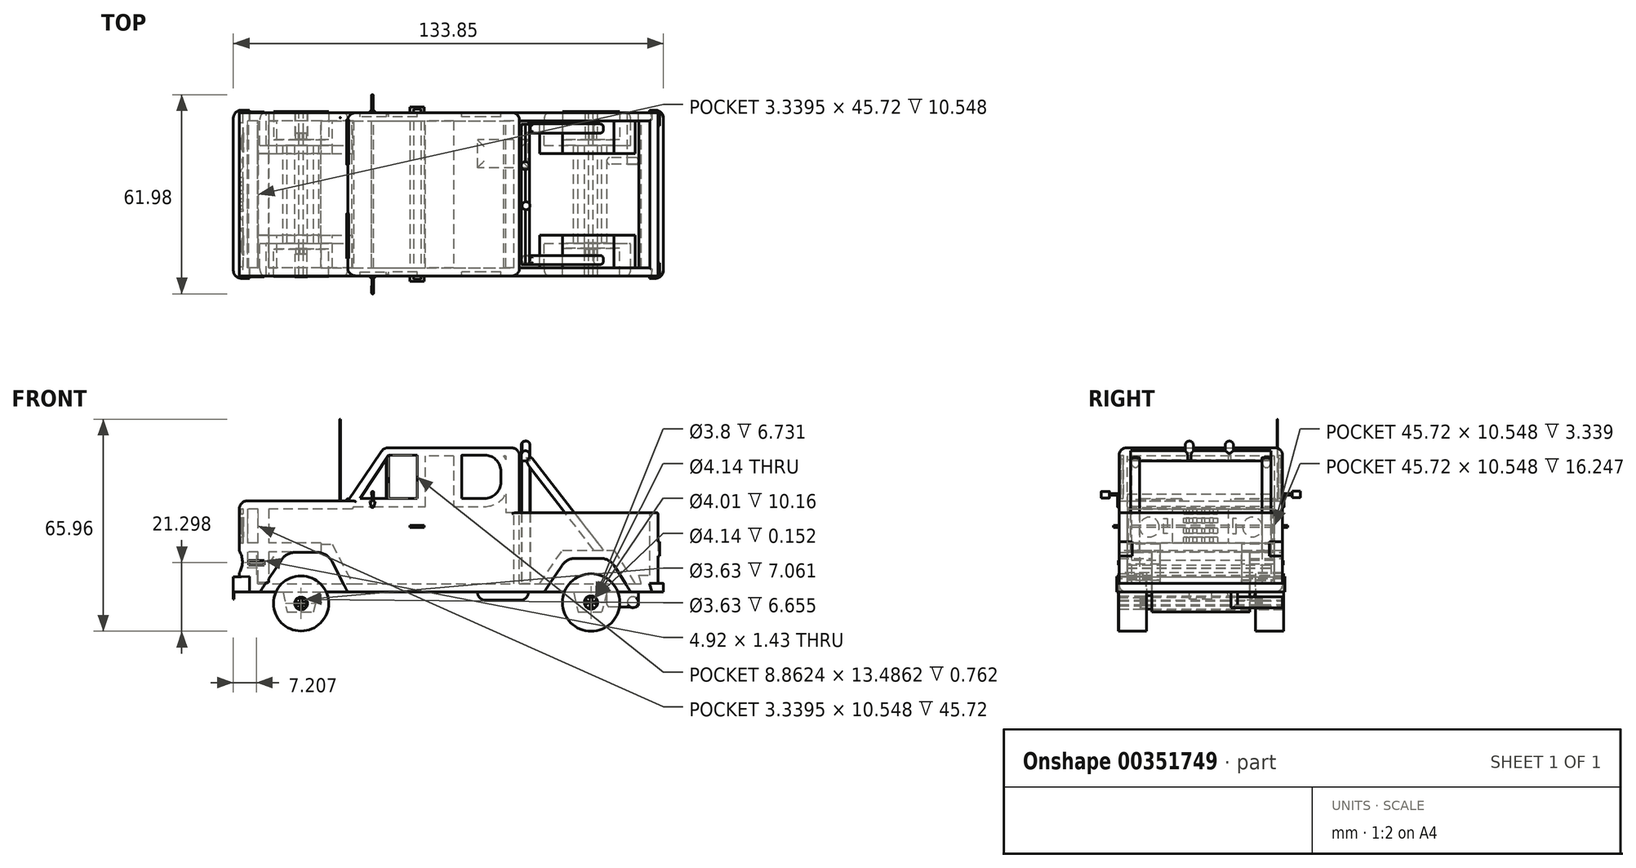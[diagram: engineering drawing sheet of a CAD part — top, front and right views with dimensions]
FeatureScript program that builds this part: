
annotation { "Feature Type Name" : "Feature", "Feature Type Description" : "" }
export const myFeature = defineFeature(function(context is Context, id is Id, definition is map)
    precondition{}
    {
        {
            var Q0;
            Q0=qCreatedBy(makeId("Front.planeOp"),FACE);
            var sketch = newSketch(context, id + "F0", { "sketchPlane" : qUnion([Q0])});
            skLineSegment(sketch, "E0", {"start": v(0, 0) * mm, "end": v(61.08, 0) * mm});
            skLineSegment(sketch, "E1", {"start": v(61.08, 0) * mm, "end": v(68.16, 10.52) * mm});
            skLineSegment(sketch, "E2", {"start": v(68.16, 10.52) * mm, "end": v(81.45, 10.52) * mm});
            skLineSegment(sketch, "E3", {"start": v(81.45, 10.52) * mm, "end": v(88.1, 0) * mm});
            skLineSegment(sketch, "E4", {"start": v(88.1, 0) * mm, "end": v(96.5, 0) * mm});
            skLineSegment(sketch, "E5", {"start": v(96.5, 0) * mm, "end": v(96.5, 24.7) * mm});
            skLineSegment(sketch, "E6", {"start": v(96.5, 24.7) * mm, "end": v(51.78, 24.7) * mm});
            skLineSegment(sketch, "E7", {"start": v(51.78, 44.9) * mm, "end": v(11.24, 44.9) * mm});
            skLineSegment(sketch, "E8", {"start": v(11.24, 44.9) * mm, "end": v(0, 28.4) * mm});
            skLineSegment(sketch, "E9", {"start": v(0, 28.4) * mm, "end": v(-33.75, 28.4) * mm});
            skLineSegment(sketch, "E10", {"start": v(-33.75, 28.4) * mm, "end": v(-33.75, 0) * mm});
            skLineSegment(sketch, "E11", {"start": v(-33.75, 0) * mm, "end": v(-27.38, 0) * mm});
            skLineSegment(sketch, "E12", {"start": v(-27.38, 0) * mm, "end": v(-19.06, 12.35) * mm});
            skPoint(sketch, "E12.endSnap0", {"position": v(96.5, 12.35) * mm});
            skLineSegment(sketch, "E13", {"start": v(-19.06, 12.35) * mm, "end": v(-6.38, 12.35) * mm});
            skLineSegment(sketch, "E14", {"start": v(-6.38, 12.35) * mm, "end": v(0, 0) * mm});
            skLineSegment(sketch, "E15", {"start": v(51.78, 44.9) * mm, "end": v(51.78, 0) * mm});
            skLineSegment(sketch, "E16", {"start": v(61.08, 0) * mm, "end": v(88.1, 0) * mm});
            skLineSegment(sketch, "E17", {"start": v(-27.38, 0) * mm, "end": v(0, 0) * mm});
            skLineSegment(sketch, "E18", {"start": v(93.9, 2.7) * mm, "end": v(98.24, 2.7) * mm});
            skLineSegment(sketch, "E19", {"start": v(98.24, 0) * mm, "end": v(94.66, 0) * mm});
            skLineSegment(sketch, "E20", {"start": v(94.66, 0) * mm, "end": v(93.9, 2.7) * mm});
            skArc(sketch, "E21", {"start": v(98.24, 2.7) * mm, "mid": v(98.15, 1.35) * mm, "end": v(98.24, 0) * mm});
            skLineSegment(sketch, "E22", {"start": v(-33.75, 4.77) * mm, "end": v(-35.61, 4.77) * mm});
            skLineSegment(sketch, "E23", {"start": v(-35.61, 4.77) * mm, "end": v(-35.61, 0) * mm});
            skLineSegment(sketch, "E24", {"start": v(-35.61, 0) * mm, "end": v(-30.56, 0) * mm});
            skLineSegment(sketch, "E25", {"start": v(-30.56, 0) * mm, "end": v(-30.56, 4.9) * mm});
            skLineSegment(sketch, "E26", {"start": v(-30.56, 4.9) * mm, "end": v(-33.75, 4.77) * mm});
            skLineSegment(sketch, "E27", {"start": v(12.77, 42.65) * mm, "end": v(3.9, 29.17) * mm});
            skLineSegment(sketch, "E28", {"start": v(3.9, 29.17) * mm, "end": v(21.63, 29.17) * mm});
            skLineSegment(sketch, "E29", {"start": v(21.63, 29.17) * mm, "end": v(21.63, 42.65) * mm});
            skLineSegment(sketch, "E30", {"start": v(21.63, 42.65) * mm, "end": v(12.77, 42.65) * mm});
            skLineSegment(sketch, "E31", {"start": v(35.5, 42.65) * mm, "end": v(35.5, 29.17) * mm});
            skLineSegment(sketch, "E32", {"start": v(35.5, 29.17) * mm, "end": v(42.56, 29.17) * mm});
            skLineSegment(sketch, "E33", {"start": v(47.64, 34.25) * mm, "end": v(47.64, 37.57) * mm});
            skLineSegment(sketch, "E34", {"start": v(42.56, 42.65) * mm, "end": v(35.5, 42.65) * mm});
            skPoint(sketch, "E35.visualSharp", {"position": v(47.64, 42.65) * mm});
            skArc(sketch, "E35.filletArc", {"start": v(47.64, 37.57) * mm, "mid": v(46.15, 41.17) * mm, "end": v(42.56, 42.65) * mm});
            skPoint(sketch, "E36.visualSharp", {"position": v(47.64, 29.17) * mm});
            skArc(sketch, "E36.filletArc", {"start": v(42.56, 29.17) * mm, "mid": v(46.15, 30.66) * mm, "end": v(47.64, 34.25) * mm});
            skSolve(sketch);
        }
        {
            var Q0;
            {var subQ2=sQuery(id+"F0.wireOp",EDGE,"E7");Q0=makeQuery(id+"F0.imprint","IMPRINT",FACE,{"disambiguationData":[TD([[makeQuery(id+"F0.imprint","IMPRINT",EDGE,{"derivedFrom":subQ2}),1.0]])]});}
            var Q1;
            {var subQ0=sQuery(id+"F0.wireOp",EDGE,"E1");Q1=makeQuery(id+"F0.imprint","IMPRINT",FACE,{"disambiguationData":[TD([[makeQuery(id+"F0.imprint","IMPRINT",EDGE,{"derivedFrom":subQ0}),1.0]])]});}
            extrude(context, id + "F1", {"entities" : qUnion([Q0, Q1]), "depth" : 25.4 * mm});
        }
        {
            var Q0;
            {var subQ2=sQuery(id+"F0.wireOp",EDGE,"E7");Q0=makeQuery(id+"F0.imprint","IMPRINT",FACE,{"disambiguationData":[TD([[makeQuery(id+"F0.imprint","IMPRINT",EDGE,{"derivedFrom":subQ2}),1.0]])]});}
            var Q1;
            {var subQ0=sQuery(id+"F0.wireOp",EDGE,"E1");Q1=makeQuery(id+"F0.imprint","IMPRINT",FACE,{"disambiguationData":[TD([[makeQuery(id+"F0.imprint","IMPRINT",EDGE,{"derivedFrom":subQ0}),1.0]])]});}
            extrude(context, id + "F2", {"entities" : qUnion([Q0, Q1]), "operationType" : NewBodyOperationType.ADD, "oppositeDirection" : true, "depth" : 25.4 * mm});
        }
        {
            var Q0;
            Q0=makeQuery(id+"F0.imprint","IMPRINT",FACE,{"disambiguationData":[TD([[makeQuery(id+"F0.imprint","IMPRINT",EDGE,{"derivedFrom":sQuery(id+"F0.wireOp",EDGE,"E12")}),-1.0]])]});
            var Q1;
            Q1=makeQuery(id+"F0.imprint","IMPRINT",FACE,{"disambiguationData":[TD([[makeQuery(id+"F0.imprint","IMPRINT",EDGE,{"derivedFrom":sQuery(id+"F0.wireOp",EDGE,"E1")}),-1.0]])]});
            var Q2;
            Q2 = qSketchRegion(id + "F8", true);
            extrude(context, id + "F3", {"entities" : qUnion([Q0, Q1, Q2]), "operationType" : NewBodyOperationType.ADD, "depth" : 15.24 * mm});
        }
        {
            var Q0;
            Q0=makeQuery(id+"F0.imprint","IMPRINT",FACE,{"disambiguationData":[TD([[makeQuery(id+"F0.imprint","IMPRINT",EDGE,{"derivedFrom":sQuery(id+"F0.wireOp",EDGE,"E12")}),-1.0]])]});
            var Q1;
            Q1=makeQuery(id+"F0.imprint","IMPRINT",FACE,{"disambiguationData":[TD([[makeQuery(id+"F0.imprint","IMPRINT",EDGE,{"derivedFrom":sQuery(id+"F0.wireOp",EDGE,"E1")}),-1.0]])]});
            extrude(context, id + "F4", {"entities" : qUnion([Q0, Q1]), "operationType" : NewBodyOperationType.ADD, "oppositeDirection" : true, "depth" : 15.24 * mm});
        }
        {
            var Q0;
            {var subQ0=sQuery(id+"F0.wireOp",EDGE,"E6");Q0=makeQuery(id+"F2.boolean.opBoolean","MERGE",FACE,{"derivedFrom":[makeQuery(id+"F1.opExtrude","SWEPT_FACE",FACE,{"disambiguationData":[OSD([subQ0])]}),makeQuery(id+"F2.opExtrude","SWEPT_FACE",FACE,{"disambiguationData":[OSD([subQ0])]})]});}
            shell(context, id + "F5", {"entities" : qUnion([Q0]), "thickness" : 2.54 * mm});
        }
        {
            var Q0;
            {var subQ0=sQuery(id+"F0.wireOp",EDGE,"E7");Q0=makeQuery(id+"F2.boolean.opBoolean","MERGE",FACE,{"derivedFrom":[makeQuery(id+"F1.opExtrude","SWEPT_FACE",FACE,{"disambiguationData":[OSD([subQ0])]}),makeQuery(id+"F2.opExtrude","SWEPT_FACE",FACE,{"disambiguationData":[OSD([subQ0])]})]});}
            var sketch = newSketch(context, id + "F6", { "sketchPlane" : qUnion([Q0])});
            skLineSegment(sketch, "E37", {"start": v(51.78, 25.4) * mm, "end": v(51.78, -25.4) * mm});
            skLineSegment(sketch, "E38", {"start": v(51.78, -25.4) * mm, "end": v(53.43, -25.4) * mm});
            skLineSegment(sketch, "E39", {"start": v(53.43, -25.4) * mm, "end": v(53.43, 25.4) * mm});
            skLineSegment(sketch, "E40", {"start": v(53.43, 25.4) * mm, "end": v(51.78, 25.4) * mm});
            skSolve(sketch);
        }
        {
            var Q0;
            Q0=makeQuery(id+"F6.imprint","IMPRINT",FACE,{"disambiguationData":[TD([[makeQuery(id+"F6.imprint","IMPRINT",EDGE,{"derivedFrom":sQuery(id+"F6.wireOp",EDGE,"E37")}),-1.0]])]});
            extrude(context, id + "F7", {"entities" : qUnion([Q0]), "operationType" : NewBodyOperationType.ADD, "oppositeDirection" : true, "depth" : 43.18 * mm});
        }
        {
            var Q0;
            {var subQ0=sQuery(id+"F0.wireOp",EDGE,"E5");Q0=makeQuery(id+"F2.boolean.opBoolean","MERGE",FACE,{"derivedFrom":[makeQuery(id+"F1.opExtrude","SWEPT_FACE",FACE,{"disambiguationData":[OSD([subQ0])]}),makeQuery(id+"F2.opExtrude","SWEPT_FACE",FACE,{"disambiguationData":[OSD([subQ0])]})]});}
            var sketch = newSketch(context, id + "F8", { "sketchPlane" : qUnion([Q0])});
            skLineSegment(sketch, "E41", {"start": v(25.4, 15.72) * mm, "end": v(21.36, 15.72) * mm});
            skLineSegment(sketch, "E42", {"start": v(21.36, 15.72) * mm, "end": v(21.36, 14.13) * mm});
            skLineSegment(sketch, "E43", {"start": v(21.36, 14.13) * mm, "end": v(25.4, 14.13) * mm});
            skLineSegment(sketch, "E44", {"start": v(25.4, 14.13) * mm, "end": v(25.4, 15.72) * mm});
            skLineSegment(sketch, "E45", {"start": v(25.4, 14.13) * mm, "end": v(25.4, 11.25) * mm});
            skLineSegment(sketch, "E46", {"start": v(25.4, 11.25) * mm, "end": v(21.36, 11.25) * mm});
            skLineSegment(sketch, "E47", {"start": v(21.36, 11.25) * mm, "end": v(21.36, 14.13) * mm});
            skLineSegment(sketch, "E48", {"start": v(-25.4, 15.72) * mm, "end": v(-21.36, 15.72) * mm});
            skLineSegment(sketch, "E49", {"start": v(-21.36, 15.72) * mm, "end": v(-21.36, 14.13) * mm});
            skLineSegment(sketch, "E50", {"start": v(-21.36, 14.13) * mm, "end": v(-25.4, 14.13) * mm});
            skLineSegment(sketch, "E51", {"start": v(-25.4, 14.13) * mm, "end": v(-25.4, 15.72) * mm});
            skLineSegment(sketch, "E52", {"start": v(-25.4, 14.13) * mm, "end": v(-25.4, 11.25) * mm});
            skLineSegment(sketch, "E53", {"start": v(-25.4, 11.25) * mm, "end": v(-21.36, 11.25) * mm});
            skLineSegment(sketch, "E54", {"start": v(-21.36, 11.25) * mm, "end": v(-21.36, 14.13) * mm});
            skSolve(sketch);
        }
        {
            var Q0;
            Q0=makeQuery(id+"F8.imprint","IMPRINT",FACE,{"disambiguationData":[TD([[makeQuery(id+"F8.imprint","IMPRINT",EDGE,{"derivedFrom":sQuery(id+"F8.wireOp",EDGE,"E43")}),-1.0]])]});
            var Q1;
            Q1=makeQuery(id+"F8.imprint","IMPRINT",FACE,{"disambiguationData":[TD([[makeQuery(id+"F8.imprint","IMPRINT",EDGE,{"derivedFrom":sQuery(id+"F8.wireOp",EDGE,"E41")}),1.0]])]});
            var Q2;
            Q2=makeQuery(id+"F8.imprint","IMPRINT",FACE,{"disambiguationData":[TD([[makeQuery(id+"F8.imprint","IMPRINT",EDGE,{"derivedFrom":sQuery(id+"F8.wireOp",EDGE,"E48")}),-1.0]])]});
            var Q3;
            Q3=makeQuery(id+"F8.imprint","IMPRINT",FACE,{"disambiguationData":[TD([[makeQuery(id+"F8.imprint","IMPRINT",EDGE,{"derivedFrom":sQuery(id+"F8.wireOp",EDGE,"E50")}),1.0]])]});
            extrude(context, id + "F9", {"entities" : qUnion([Q0, Q1, Q2, Q3]), "operationType" : NewBodyOperationType.ADD, "depth" : 0.5 * mm});
        }
        {
            var Q0;
            {var subQ5=sQuery(id+"F0.wireOp",EDGE,"E21");Q0=makeQuery(id+"F0.imprint","IMPRINT",FACE,{"disambiguationData":[TD([[makeQuery(id+"F0.imprint","IMPRINT",EDGE,{"derivedFrom":subQ5}),-1.0]])]});}
            var Q1;
            {var subQ5=sQuery(id+"F0.wireOp",EDGE,"E20");Q1=makeQuery(id+"F0.imprint","IMPRINT",FACE,{"disambiguationData":[TD([[makeQuery(id+"F0.imprint","IMPRINT",EDGE,{"derivedFrom":subQ5}),-1.0]])]});}
            extrude(context, id + "F10", {"entities" : qUnion([Q0, Q1]), "operationType" : NewBodyOperationType.ADD, "depth" : 26.16 * mm});
        }
        {
            var Q0;
            {var subQ5=sQuery(id+"F0.wireOp",EDGE,"E20");Q0=makeQuery(id+"F0.imprint","IMPRINT",FACE,{"disambiguationData":[TD([[makeQuery(id+"F0.imprint","IMPRINT",EDGE,{"derivedFrom":subQ5}),-1.0]])]});}
            var Q1;
            {var subQ5=sQuery(id+"F0.wireOp",EDGE,"E21");Q1=makeQuery(id+"F0.imprint","IMPRINT",FACE,{"disambiguationData":[TD([[makeQuery(id+"F0.imprint","IMPRINT",EDGE,{"derivedFrom":subQ5}),-1.0]])]});}
            extrude(context, id + "F11", {"entities" : qUnion([Q0, Q1]), "operationType" : NewBodyOperationType.ADD, "oppositeDirection" : true, "depth" : 26.16 * mm});
        }
        {
            var Q0;
            Q0=makeQuery(id+"F11.opExtrude","CAP_EDGE",EDGE,{"disambiguationData":[OSD([sQuery(id+"F0.wireOp",EDGE,"E21")])],"isStart":false});
            var Q1;
            Q1=makeQuery(id+"F10.opExtrude","CAP_EDGE",EDGE,{"disambiguationData":[OSD([sQuery(id+"F0.wireOp",EDGE,"E21")])],"isStart":false});
            fillet(context, id + "F12", {"entities" : qUnion([Q0, Q1]), "radius" : 2.54 * mm, "tangentPropagation" : true, "allowEdgeOverflow" : false});
        }
        {
            var Q0;
            {var subQ4=sQuery(id+"F0.wireOp",EDGE,"E25");Q0=makeQuery(id+"F0.imprint","IMPRINT",FACE,{"disambiguationData":[TD([[makeQuery(id+"F0.imprint","IMPRINT",EDGE,{"derivedFrom":subQ4}),1.0]])]});}
            var Q1;
            {var subQ3=sQuery(id+"F0.wireOp",EDGE,"E22");Q1=makeQuery(id+"F0.imprint","IMPRINT",FACE,{"disambiguationData":[TD([[makeQuery(id+"F0.imprint","IMPRINT",EDGE,{"derivedFrom":subQ3}),1.0]])]});}
            extrude(context, id + "F13", {"entities" : qUnion([Q0, Q1]), "operationType" : NewBodyOperationType.ADD, "depth" : 26.16 * mm});
        }
        {
            var Q0;
            {var subQ4=sQuery(id+"F0.wireOp",EDGE,"E25");Q0=makeQuery(id+"F0.imprint","IMPRINT",FACE,{"disambiguationData":[TD([[makeQuery(id+"F0.imprint","IMPRINT",EDGE,{"derivedFrom":subQ4}),1.0]])]});}
            var Q1;
            {var subQ3=sQuery(id+"F0.wireOp",EDGE,"E22");Q1=makeQuery(id+"F0.imprint","IMPRINT",FACE,{"disambiguationData":[TD([[makeQuery(id+"F0.imprint","IMPRINT",EDGE,{"derivedFrom":subQ3}),1.0]])]});}
            extrude(context, id + "F14", {"entities" : qUnion([Q0, Q1]), "operationType" : NewBodyOperationType.ADD, "oppositeDirection" : true, "depth" : 26.16 * mm});
        }
        {
            var Q0;
            Q0=makeQuery(id+"F14.opExtrude","CAP_EDGE",EDGE,{"disambiguationData":[OSD([sQuery(id+"F0.wireOp",EDGE,"E23")])],"isStart":false});
            var Q1;
            Q1=makeQuery(id+"F13.opExtrude","CAP_EDGE",EDGE,{"disambiguationData":[OSD([sQuery(id+"F0.wireOp",EDGE,"E23")])],"isStart":false});
            fillet(context, id + "F15", {"entities" : qUnion([Q0, Q1]), "radius" : 2.54 * mm, "tangentPropagation" : true, "allowEdgeOverflow" : false});
        }
        {
            var Q0;
            Q0=makeQuery(id+"F7.opExtrude","CAP_EDGE",EDGE,{"disambiguationData":[OSD([sQuery(id+"F6.wireOp",EDGE,"E39")])],"isStart":true});
            var Q1;
            {var subQ0=sQuery(id+"F0.wireOp",EDGE,"E8");var subQ1=sQuery(id+"F0.wireOp",EDGE,"E7");Q1=makeQuery(id+"F2.boolean.opBoolean","MERGE",EDGE,{"derivedFrom":[makeQuery(id+"F1.opExtrude","SWEPT_EDGE",EDGE,{"disambiguationData":[OSD([subQ1,subQ0])]}),makeQuery(id+"F2.opExtrude","SWEPT_EDGE",EDGE,{"disambiguationData":[OSD([subQ1,subQ0])]})]});}
            var Q2;
            {var subQ0=sQuery(id+"F0.wireOp",EDGE,"E10");var subQ1=sQuery(id+"F0.wireOp",EDGE,"E9");Q2=makeQuery(id+"F2.boolean.opBoolean","MERGE",EDGE,{"derivedFrom":[makeQuery(id+"F1.opExtrude","SWEPT_EDGE",EDGE,{"disambiguationData":[OSD([subQ1,subQ0])]}),makeQuery(id+"F2.opExtrude","SWEPT_EDGE",EDGE,{"disambiguationData":[OSD([subQ1,subQ0])]})]});}
            fillet(context, id + "F16", {"entities" : qUnion([Q0, Q1, Q2]), "radius" : 2.54 * mm, "tangentPropagation" : true, "allowEdgeOverflow" : false});
        }
        {
            var Q0;
            Q0=makeQuery(id+"F0.imprint","IMPRINT",FACE,{"disambiguationData":[TD([[makeQuery(id+"F0.imprint","IMPRINT",EDGE,{"derivedFrom":sQuery(id+"F0.wireOp",EDGE,"E27")}),1.0]])]});
            var Q1;
            Q1=makeQuery(id+"F0.imprint","IMPRINT",FACE,{"disambiguationData":[TD([[makeQuery(id+"F0.imprint","IMPRINT",EDGE,{"derivedFrom":sQuery(id+"F0.wireOp",EDGE,"E31")}),1.0]])]});
            extrude(context, id + "F17", {"entities" : qUnion([Q0, Q1]), "operationType" : NewBodyOperationType.ADD, "oppositeDirection" : true, "depth" : 24.13 * mm});
        }
        {
            var Q0;
            Q0=makeQuery(id+"F0.imprint","IMPRINT",FACE,{"disambiguationData":[TD([[makeQuery(id+"F0.imprint","IMPRINT",EDGE,{"derivedFrom":sQuery(id+"F0.wireOp",EDGE,"E27")}),1.0]])]});
            var Q1;
            Q1=makeQuery(id+"F0.imprint","IMPRINT",FACE,{"disambiguationData":[TD([[makeQuery(id+"F0.imprint","IMPRINT",EDGE,{"derivedFrom":sQuery(id+"F0.wireOp",EDGE,"E31")}),1.0]])]});
            extrude(context, id + "F18", {"entities" : qUnion([Q0, Q1]), "operationType" : NewBodyOperationType.ADD, "depth" : 24.13 * mm});
        }
        {
            var Q0;
            {var subQ0=sQuery(id+"F0.wireOp",EDGE,"E10");Q0=makeQuery(id+"F2.boolean.opBoolean","MERGE",FACE,{"derivedFrom":[makeQuery(id+"F1.opExtrude","SWEPT_FACE",FACE,{"disambiguationData":[OSD([subQ0])]}),makeQuery(id+"F2.opExtrude","SWEPT_FACE",FACE,{"disambiguationData":[OSD([subQ0])]})]});}
            var sketch = newSketch(context, id + "F19", { "sketchPlane" : qUnion([Q0])});
            skLineSegment(sketch, "E55.top", {"start": v(-25.4, 25.86) * mm, "end": v(25.4, 25.86) * mm});
            skLineSegment(sketch, "E56", {"start": v(25.4, 25.86) * mm, "end": v(25.4, 15.31) * mm});
            skLineSegment(sketch, "E57", {"start": v(25.4, 15.31) * mm, "end": v(-25.4, 15.31) * mm});
            skLineSegment(sketch, "E58", {"start": v(-25.4, 15.31) * mm, "end": v(-25.4, 25.86) * mm});
            skSolve(sketch);
        }
        {
            var Q0;
            Q0=makeQuery(id+"F19.imprint","IMPRINT",FACE,{"disambiguationData":[TD([[makeQuery(id+"F19.imprint","IMPRINT",EDGE,{"derivedFrom":sQuery(id+"F19.wireOp",EDGE,"E55.top")}),1.0]])]});
            extrude(context, id + "F20", {"entities" : qUnion([Q0]), "operationType" : NewBodyOperationType.REMOVE, "oppositeDirection" : true, "depth" : 1.27 * mm});
        }
        {
            var Q0;
            {var subQ0=sQuery(id+"F0.wireOp",EDGE,"E9");Q0=makeQuery(id+"F2.boolean.opBoolean","MERGE",FACE,{"derivedFrom":[makeQuery(id+"F1.opExtrude","SWEPT_FACE",FACE,{"disambiguationData":[OSD([subQ0])]}),makeQuery(id+"F2.opExtrude","SWEPT_FACE",FACE,{"disambiguationData":[OSD([subQ0])]})]});}
            var sketch = newSketch(context, id + "F21", { "sketchPlane" : qUnion([Q0])});
            skLineSegment(sketch, "E59", {"start": v(-27.87, -25.4) * mm, "end": v(-27.87, 25.4) * mm});
            skLineSegment(sketch, "E60", {"start": v(-27.87, 25.4) * mm, "end": v(-24.6, 25.4) * mm});
            skLineSegment(sketch, "E61", {"start": v(-24.6, 25.4) * mm, "end": v(-24.6, -25.4) * mm});
            skLineSegment(sketch, "E62", {"start": v(-24.6, -25.4) * mm, "end": v(-27.87, -25.4) * mm});
            skSolve(sketch);
        }
        {
            var Q0;
            Q0=makeQuery(id+"F21.imprint","IMPRINT",FACE,{"disambiguationData":[TD([[makeQuery(id+"F21.imprint","IMPRINT",EDGE,{"derivedFrom":sQuery(id+"F21.wireOp",EDGE,"E59")}),-1.0]])]});
            extrude(context, id + "F22", {"entities" : qUnion([Q0]), "operationType" : NewBodyOperationType.ADD, "oppositeDirection" : true, "depth" : 25.4 * mm});
        }
        {
            var Q0;
            {var subQ0=sQuery(id+"F0.wireOp",EDGE,"E10");Q0=makeQuery(id+"F2.boolean.opBoolean","MERGE",FACE,{"derivedFrom":[makeQuery(id+"F1.opExtrude","SWEPT_FACE",FACE,{"disambiguationData":[OSD([subQ0])]}),makeQuery(id+"F2.opExtrude","SWEPT_FACE",FACE,{"disambiguationData":[OSD([subQ0])]})]});}
            var sketch = newSketch(context, id + "F23", { "sketchPlane" : qUnion([Q0])});
            skLineSegment(sketch, "E63", {"start": v(-25.4, 15.31) * mm, "end": v(25.4, 15.31) * mm});
            skLineSegment(sketch, "E64", {"start": v(25.4, 15.31) * mm, "end": v(25.4, 12.44) * mm});
            skLineSegment(sketch, "E65", {"start": v(25.4, 12.44) * mm, "end": v(-25.4, 12.44) * mm});
            skLineSegment(sketch, "E66", {"start": v(-25.4, 12.44) * mm, "end": v(-25.4, 15.31) * mm});
            skSolve(sketch);
        }
        {
            var Q0;
            Q0=makeQuery(id+"F23.imprint","IMPRINT",FACE,{"disambiguationData":[TD([[makeQuery(id+"F23.imprint","IMPRINT",EDGE,{"derivedFrom":sQuery(id+"F23.wireOp",EDGE,"E63")}),1.0]])]});
            extrude(context, id + "F24", {"entities" : qUnion([Q0]), "operationType" : NewBodyOperationType.ADD, "oppositeDirection" : true, "depth" : 25.4 * mm});
        }
        {
            var Q0;
            Q0=makeQuery(id+"F20.boolean.opBoolean","COPY",FACE,{"derivedFrom":makeQuery(id+"F20.opExtrude","CAP_FACE",FACE,{"disambiguationData":[OSD([sQuery(id+"F19.wireOp",EDGE,"E55.top"),sQuery(id+"F19.wireOp",EDGE,"E56"),sQuery(id+"F19.wireOp",EDGE,"E57"),sQuery(id+"F19.wireOp",EDGE,"E58")])],"isStart":false})});
            var sketch = newSketch(context, id + "F25", { "sketchPlane" : qUnion([Q0])});
            skLineSegment(sketch, "E67", {"start": v(25.4, 25.86) * mm, "end": v(25.4, 15.31) * mm});
            skLineSegment(sketch, "E68", {"start": v(25.4, 15.31) * mm, "end": v(22.54, 15.31) * mm});
            skLineSegment(sketch, "E69", {"start": v(22.54, 15.31) * mm, "end": v(22.54, 25.86) * mm});
            skLineSegment(sketch, "E70", {"start": v(22.54, 25.86) * mm, "end": v(25.4, 25.86) * mm});
            skLineSegment(sketch, "E71", {"start": v(-25.4, 25.86) * mm, "end": v(-22.36, 25.86) * mm});
            skLineSegment(sketch, "E72", {"start": v(-22.36, 25.86) * mm, "end": v(-22.36, 15.31) * mm});
            skLineSegment(sketch, "E73", {"start": v(-22.36, 15.31) * mm, "end": v(-25.4, 15.31) * mm});
            skLineSegment(sketch, "E74", {"start": v(-25.4, 15.31) * mm, "end": v(-25.4, 25.86) * mm});
            skLineSegment(sketch, "E75", {"start": v(8.71, 25.86) * mm, "end": v(-8.54, 25.86) * mm});
            skLineSegment(sketch, "E76", {"start": v(-8.54, 25.86) * mm, "end": v(-8.54, 15.31) * mm});
            skLineSegment(sketch, "E77", {"start": v(-8.54, 15.31) * mm, "end": v(8.71, 15.31) * mm});
            skLineSegment(sketch, "E78", {"start": v(8.71, 15.31) * mm, "end": v(8.71, 25.86) * mm});
            skSolve(sketch);
        }
        {
            var Q0;
            Q0=makeQuery(id+"F25.imprint","IMPRINT",FACE,{"disambiguationData":[TD([[makeQuery(id+"F25.imprint","IMPRINT",EDGE,{"derivedFrom":sQuery(id+"F25.wireOp",EDGE,"E75")}),1.0]])]});
            var Q1;
            Q1=makeQuery(id+"F25.imprint","IMPRINT",FACE,{"disambiguationData":[TD([[makeQuery(id+"F25.imprint","IMPRINT",EDGE,{"derivedFrom":sQuery(id+"F25.wireOp",EDGE,"E71")}),1.0]])]});
            var Q2;
            Q2=makeQuery(id+"F25.imprint","IMPRINT",FACE,{"disambiguationData":[TD([[makeQuery(id+"F25.imprint","IMPRINT",EDGE,{"derivedFrom":sQuery(id+"F25.wireOp",EDGE,"E67")}),-1.0]])]});
            extrude(context, id + "F26", {"entities" : qUnion([Q0, Q1, Q2]), "operationType" : NewBodyOperationType.ADD, "depth" : 1.27 * mm});
        }
        {
            var Q0;
            Q0=makeQuery(id+"F26.opExtrude","CAP_EDGE",EDGE,{"disambiguationData":[OSD([sQuery(id+"F25.wireOp",EDGE,"E78")])],"isStart":false});
            var Q1;
            Q1=makeQuery(id+"F26.opExtrude","CAP_EDGE",EDGE,{"disambiguationData":[OSD([sQuery(id+"F25.wireOp",EDGE,"E76")])],"isStart":false});
            fillet(context, id + "F27", {"entities" : qUnion([Q0, Q1]), "radius" : 5.08 * mm, "tangentPropagation" : true, "allowEdgeOverflow" : false});
        }
        {
            var Q0;
            {var subQ0=sQuery(id+"F19.wireOp",EDGE,"E55.top");var subQ1=sQuery(id+"F19.wireOp",EDGE,"E57");Q0=makeQuery(id+"F26.boolean.opBoolean","SPLIT",FACE,{"disambiguationData":[TD([makeQuery(id+"F26.opExtrude","SWEPT_FACE",FACE,{"disambiguationData":[OSD([sQuery(id+"F25.wireOp",EDGE,"E72")])]})])],"derivedFrom":makeQuery(id+"F20.boolean.opBoolean","COPY",FACE,{"derivedFrom":makeQuery(id+"F20.opExtrude","CAP_FACE",FACE,{"disambiguationData":[OSD([subQ0,sQuery(id+"F19.wireOp",EDGE,"E56"),subQ1,sQuery(id+"F19.wireOp",EDGE,"E58")])],"isStart":false})})});}
            var sketch = newSketch(context, id + "F28", { "sketchPlane" : qUnion([Q0])});
            skCircle(sketch, "E79", {"center": v(-16.07, 20.25) * mm, "radius": 3.06 * mm});
            skCircle(sketch, "E80", {"center": v(15.98, 20.25) * mm, "radius": 3.07 * mm});
            skLineSegment(sketch, "E81", {"start": v(11.56, 22.94) * mm, "end": v(10.42, 22.94) * mm});
            skLineSegment(sketch, "E82", {"start": v(10.42, 22.94) * mm, "end": v(10.42, 18.22) * mm});
            skLineSegment(sketch, "E83", {"start": v(10.42, 18.22) * mm, "end": v(11.56, 18.22) * mm});
            skLineSegment(sketch, "E84", {"start": v(11.56, 18.22) * mm, "end": v(11.56, 22.94) * mm});
            skLineSegment(sketch, "E85", {"start": v(-9.85, 22.94) * mm, "end": v(-9.85, 18.22) * mm});
            skLineSegment(sketch, "E86", {"start": v(-9.85, 18.22) * mm, "end": v(-11, 18.22) * mm});
            skLineSegment(sketch, "E87", {"start": v(-11, 18.22) * mm, "end": v(-11, 22.94) * mm});
            skLineSegment(sketch, "E88", {"start": v(-11, 22.94) * mm, "end": v(-9.85, 22.94) * mm});
            skSolve(sketch);
        }
        {
            var Q0;
            Q0=makeQuery(id+"F28.imprint","IMPRINT",FACE,{"disambiguationData":[TD([[makeQuery(id+"F28.imprint","IMPRINT",EDGE,{"derivedFrom":sQuery(id+"F28.wireOp",EDGE,"8cGmHD0W-AUDj-nJp2-IjLW-vJfDeqEBS3v5")}),1.0]])]});
            var Q1;
            Q1=makeQuery(id+"F28.imprint","IMPRINT",FACE,{"disambiguationData":[TD([[makeQuery(id+"F28.imprint","IMPRINT",EDGE,{"derivedFrom":sQuery(id+"F28.wireOp",EDGE,"9dRMdp0R-Xc4K-p7fW-M7a4-LUDvDldkzqLd")}),1.0]])]});
            var Q2;
            Q2=makeQuery(id+"F28.imprint","IMPRINT",FACE,{"disambiguationData":[TD([[makeQuery(id+"F28.imprint","IMPRINT",EDGE,{"derivedFrom":sQuery(id+"F28.wireOp",EDGE,"E79")}),1.0]])]});
            var Q3;
            Q3=makeQuery(id+"F28.imprint","IMPRINT",FACE,{"disambiguationData":[TD([[makeQuery(id+"F28.imprint","IMPRINT",EDGE,{"derivedFrom":sQuery(id+"F28.wireOp",EDGE,"E85")}),-1.0]])]});
            var Q4;
            Q4=makeQuery(id+"F28.imprint","IMPRINT",FACE,{"disambiguationData":[TD([[makeQuery(id+"F28.imprint","IMPRINT",EDGE,{"derivedFrom":sQuery(id+"F28.wireOp",EDGE,"E81")}),1.0]])]});
            var Q5;
            Q5=makeQuery(id+"F28.imprint","IMPRINT",FACE,{"disambiguationData":[TD([[makeQuery(id+"F28.imprint","IMPRINT",EDGE,{"derivedFrom":sQuery(id+"F28.wireOp",EDGE,"E80")}),1.0]])]});
            extrude(context, id + "F29", {"entities" : qUnion([Q0, Q1, Q2, Q3, Q4, Q5]), "operationType" : NewBodyOperationType.ADD, "depth" : 0.5 * mm});
        }
        {
            var Q0;
            Q0=makeQuery(id+"F29.opExtrude","CAP_EDGE",EDGE,{"disambiguationData":[OSD([sQuery(id+"F28.wireOp",EDGE,"E80")])],"isStart":false});
            var Q1;
            Q1=makeQuery(id+"F29.opExtrude","CAP_EDGE",EDGE,{"disambiguationData":[OSD([sQuery(id+"F28.wireOp",EDGE,"E79")])],"isStart":false});
            fillet(context, id + "F30", {"entities" : qUnion([Q0, Q1]), "radius" : 2.54 * mm, "tangentPropagation" : true, "allowEdgeOverflow" : false});
        }
        {
            var Q0;
            {var subQ0=sQuery(id+"F0.wireOp",EDGE,"E10");Q0=makeQuery(id+"F26.boolean.opBoolean","MERGE",FACE,{"derivedFrom":[makeQuery(id+"F2.boolean.opBoolean","MERGE",FACE,{"derivedFrom":[makeQuery(id+"F1.opExtrude","SWEPT_FACE",FACE,{"disambiguationData":[OSD([subQ0])]}),makeQuery(id+"F2.opExtrude","SWEPT_FACE",FACE,{"disambiguationData":[OSD([subQ0])]})]}),makeQuery(id+"F26.opExtrude","CAP_FACE",FACE,{"disambiguationData":[OSD([sQuery(id+"F25.wireOp",EDGE,"E67"),sQuery(id+"F25.wireOp",EDGE,"E68"),sQuery(id+"F25.wireOp",EDGE,"E69"),sQuery(id+"F25.wireOp",EDGE,"E70")])],"isStart":false}),makeQuery(id+"F26.opExtrude","CAP_FACE",FACE,{"disambiguationData":[OSD([sQuery(id+"F25.wireOp",EDGE,"E71"),sQuery(id+"F25.wireOp",EDGE,"E72"),sQuery(id+"F25.wireOp",EDGE,"E73"),sQuery(id+"F25.wireOp",EDGE,"E74")])],"isStart":false}),makeQuery(id+"F26.opExtrude","CAP_FACE",FACE,{"disambiguationData":[OSD([sQuery(id+"F25.wireOp",EDGE,"E75"),sQuery(id+"F25.wireOp",EDGE,"E76"),sQuery(id+"F25.wireOp",EDGE,"E77"),sQuery(id+"F25.wireOp",EDGE,"E78")])],"isStart":false})]});}
            var sketch = newSketch(context, id + "F31", { "sketchPlane" : qUnion([Q0])});
            skLineSegment(sketch, "E89", {"start": v(-5.18, 25.86) * mm, "end": v(5.35, 25.86) * mm});
            skLineSegment(sketch, "E90", {"start": v(5.35, 25.86) * mm, "end": v(5.35, 24.3) * mm});
            skLineSegment(sketch, "E91", {"start": v(5.35, 24.3) * mm, "end": v(-5.18, 24.3) * mm});
            skLineSegment(sketch, "E92", {"start": v(-5.18, 24.3) * mm, "end": v(-5.18, 25.86) * mm});
            skLineSegment(sketch, "E93", {"start": v(5.35, 23.01) * mm, "end": v(-5.18, 23.01) * mm});
            skLineSegment(sketch, "E94", {"start": v(-5.18, 23.01) * mm, "end": v(-5.18, 21.46) * mm});
            skLineSegment(sketch, "E95", {"start": v(-5.18, 21.46) * mm, "end": v(5.35, 21.46) * mm});
            skLineSegment(sketch, "E96", {"start": v(5.35, 21.46) * mm, "end": v(5.35, 23.01) * mm});
            skLineSegment(sketch, "E97", {"start": v(-5.18, 19.91) * mm, "end": v(5.35, 19.91) * mm});
            skLineSegment(sketch, "E98", {"start": v(5.35, 19.91) * mm, "end": v(5.35, 18.36) * mm});
            skLineSegment(sketch, "E99", {"start": v(5.35, 18.36) * mm, "end": v(-5.18, 18.36) * mm});
            skLineSegment(sketch, "E100", {"start": v(-5.18, 18.36) * mm, "end": v(-5.18, 19.91) * mm});
            skLineSegment(sketch, "E101", {"start": v(-5.18, 17.07) * mm, "end": v(5.35, 17.07) * mm});
            skLineSegment(sketch, "E102", {"start": v(5.35, 17.07) * mm, "end": v(5.35, 15.31) * mm});
            skLineSegment(sketch, "E103", {"start": v(5.35, 15.31) * mm, "end": v(-5.18, 15.31) * mm});
            skLineSegment(sketch, "E104", {"start": v(-5.18, 15.31) * mm, "end": v(-5.18, 17.07) * mm});
            skSolve(sketch);
        }
        {
            var Q0;
            Q0=makeQuery(id+"F31.imprint","IMPRINT",FACE,{"disambiguationData":[TD([[makeQuery(id+"F31.imprint","IMPRINT",EDGE,{"derivedFrom":sQuery(id+"F31.wireOp",EDGE,"E89")}),1.0]])]});
            var Q1;
            Q1=makeQuery(id+"F31.imprint","IMPRINT",FACE,{"disambiguationData":[TD([[makeQuery(id+"F31.imprint","IMPRINT",EDGE,{"derivedFrom":sQuery(id+"F31.wireOp",EDGE,"E93")}),1.0]])]});
            var Q2;
            Q2=makeQuery(id+"F31.imprint","IMPRINT",FACE,{"disambiguationData":[TD([[makeQuery(id+"F31.imprint","IMPRINT",EDGE,{"derivedFrom":sQuery(id+"F31.wireOp",EDGE,"E97")}),-1.0]])]});
            var Q3;
            Q3=makeQuery(id+"F31.imprint","IMPRINT",FACE,{"disambiguationData":[TD([[makeQuery(id+"F31.imprint","IMPRINT",EDGE,{"derivedFrom":sQuery(id+"F31.wireOp",EDGE,"E101")}),-1.0]])]});
            extrude(context, id + "F32", {"entities" : qUnion([Q0, Q1, Q2, Q3]), "operationType" : NewBodyOperationType.REMOVE, "oppositeDirection" : true, "depth" : 1.12 * mm});
        }
        {
            var Q0;
            Q0=makeQuery(id+"F32.boolean.opBoolean","COPY",FACE,{"derivedFrom":makeQuery(id+"F32.opExtrude","CAP_FACE",FACE,{"disambiguationData":[OSD([sQuery(id+"F31.wireOp",EDGE,"E89"),sQuery(id+"F31.wireOp",EDGE,"E90"),sQuery(id+"F31.wireOp",EDGE,"E91"),sQuery(id+"F31.wireOp",EDGE,"E92")])],"isStart":false})});
            var sketch = newSketch(context, id + "F33", { "sketchPlane" : qUnion([Q0])});
            skLineSegment(sketch, "E105", {"start": v(-3.85, 25.86) * mm, "end": v(-3.85, 15.37) * mm});
            skLineSegment(sketch, "E106", {"start": v(-3.85, 15.37) * mm, "end": v(-2.81, 15.37) * mm});
            skLineSegment(sketch, "E107", {"start": v(-2.81, 15.37) * mm, "end": v(-2.81, 25.86) * mm});
            skLineSegment(sketch, "E108", {"start": v(-2.81, 25.86) * mm, "end": v(-3.85, 25.86) * mm});
            skLineSegment(sketch, "E109", {"start": v(-1.28, 25.86) * mm, "end": v(-0.24, 25.86) * mm});
            skLineSegment(sketch, "E110", {"start": v(-0.24, 25.86) * mm, "end": v(-0.24, 15.4) * mm});
            skLineSegment(sketch, "E111", {"start": v(-0.24, 15.4) * mm, "end": v(-1.28, 15.37) * mm});
            skLineSegment(sketch, "E112", {"start": v(-1.28, 15.37) * mm, "end": v(-1.28, 25.86) * mm});
            skLineSegment(sketch, "E113", {"start": v(1.28, 25.86) * mm, "end": v(1.28, 15.4) * mm});
            skLineSegment(sketch, "E114", {"start": v(1.28, 15.4) * mm, "end": v(2.36, 15.4) * mm});
            skLineSegment(sketch, "E115", {"start": v(2.36, 15.4) * mm, "end": v(2.36, 25.86) * mm});
            skLineSegment(sketch, "E116", {"start": v(2.36, 25.86) * mm, "end": v(1.28, 25.86) * mm});
            skLineSegment(sketch, "E117", {"start": v(3.5, 25.86) * mm, "end": v(4.6, 25.86) * mm});
            skLineSegment(sketch, "E118", {"start": v(4.6, 25.86) * mm, "end": v(4.6, 15.3) * mm});
            skLineSegment(sketch, "E119", {"start": v(4.6, 15.3) * mm, "end": v(3.5, 15.3) * mm});
            skLineSegment(sketch, "E120", {"start": v(3.5, 15.3) * mm, "end": v(3.5, 25.86) * mm});
            skSolve(sketch);
        }
        {
            var Q0;
            {var subQ0=sQuery(id+"F33.wireOp",EDGE,"E119");Q0=makeQuery(id+"F33.imprint","IMPRINT",FACE,{"disambiguationData":[TD([[makeQuery(id+"F33.imprint","IMPRINT",EDGE,{"derivedFrom":subQ0}),-1.0]])]});}
            var Q1;
            {var subQ0=sQuery(id+"F33.wireOp",EDGE,"E117");Q1=makeQuery(id+"F33.imprint","IMPRINT",FACE,{"disambiguationData":[TD([[makeQuery(id+"F33.imprint","IMPRINT",EDGE,{"derivedFrom":subQ0}),1.0]])]});}
            var Q2;
            {var subQ0=sQuery(id+"F33.wireOp",EDGE,"E114");Q2=makeQuery(id+"F33.imprint","IMPRINT",FACE,{"disambiguationData":[TD([[makeQuery(id+"F33.imprint","IMPRINT",EDGE,{"derivedFrom":subQ0}),1.0]])]});}
            var Q3;
            {var subQ0=sQuery(id+"F33.wireOp",EDGE,"E116");Q3=makeQuery(id+"F33.imprint","IMPRINT",FACE,{"disambiguationData":[TD([[makeQuery(id+"F33.imprint","IMPRINT",EDGE,{"derivedFrom":subQ0}),1.0]])]});}
            var Q4;
            {var subQ0=sQuery(id+"F33.wireOp",EDGE,"E109");Q4=makeQuery(id+"F33.imprint","IMPRINT",FACE,{"disambiguationData":[TD([[makeQuery(id+"F33.imprint","IMPRINT",EDGE,{"derivedFrom":subQ0}),1.0]])]});}
            var Q5;
            {var subQ0=sQuery(id+"F33.wireOp",EDGE,"E111");Q5=makeQuery(id+"F33.imprint","IMPRINT",FACE,{"disambiguationData":[TD([[makeQuery(id+"F33.imprint","IMPRINT",EDGE,{"derivedFrom":subQ0}),-1.0]])]});}
            var Q6;
            {var subQ0=sQuery(id+"F33.wireOp",EDGE,"E106");Q6=makeQuery(id+"F33.imprint","IMPRINT",FACE,{"disambiguationData":[TD([[makeQuery(id+"F33.imprint","IMPRINT",EDGE,{"derivedFrom":subQ0}),1.0]])]});}
            var Q7;
            {var subQ0=sQuery(id+"F33.wireOp",EDGE,"E108");Q7=makeQuery(id+"F33.imprint","IMPRINT",FACE,{"disambiguationData":[TD([[makeQuery(id+"F33.imprint","IMPRINT",EDGE,{"derivedFrom":subQ0}),1.0]])]});}
            extrude(context, id + "F34", {"entities" : qUnion([Q0, Q1, Q2, Q3, Q4, Q5, Q6, Q7]), "operationType" : NewBodyOperationType.ADD, "depth" : 0.69 * mm});
        }
        {
            var Q0;
            Q0=makeQuery(id+"F26.boolean.opBoolean","MERGE",FACE,{"derivedFrom":[makeQuery(id+"F22.boolean.opBoolean","MERGE",FACE,{"derivedFrom":[makeQuery(id+"F9.boolean.opBoolean","MERGE",FACE,{"derivedFrom":[makeQuery(id+"F7.boolean.opBoolean","MERGE",FACE,{"derivedFrom":[makeQuery(id+"F1.opExtrude","CAP_FACE",FACE,{"disambiguationData":[OSD([sQuery(id+"F0.wireOp",EDGE,"E0"),sQuery(id+"F0.wireOp",EDGE,"E1"),sQuery(id+"F0.wireOp",EDGE,"E2"),sQuery(id+"F0.wireOp",EDGE,"E3"),sQuery(id+"F0.wireOp",EDGE,"E4"),sQuery(id+"F0.wireOp",EDGE,"E5"),sQuery(id+"F0.wireOp",EDGE,"E6"),sQuery(id+"F0.wireOp",EDGE,"E7"),sQuery(id+"F0.wireOp",EDGE,"E8"),sQuery(id+"F0.wireOp",EDGE,"E9"),sQuery(id+"F0.wireOp",EDGE,"E10"),sQuery(id+"F0.wireOp",EDGE,"E11"),sQuery(id+"F0.wireOp",EDGE,"E12"),sQuery(id+"F0.wireOp",EDGE,"E13"),sQuery(id+"F0.wireOp",EDGE,"E14"),sQuery(id+"F0.wireOp",EDGE,"E15"),sQuery(id+"F0.wireOp",EDGE,"E18"),sQuery(id+"F0.wireOp",EDGE,"E20"),sQuery(id+"F0.wireOp",EDGE,"E25"),sQuery(id+"F0.wireOp",EDGE,"E26"),sQuery(id+"F0.wireOp",EDGE,"E27"),sQuery(id+"F0.wireOp",EDGE,"E28"),sQuery(id+"F0.wireOp",EDGE,"E29"),sQuery(id+"F0.wireOp",EDGE,"E30"),sQuery(id+"F0.wireOp",EDGE,"E31"),sQuery(id+"F0.wireOp",EDGE,"E32"),sQuery(id+"F0.wireOp",EDGE,"E33"),sQuery(id+"F0.wireOp",EDGE,"E34"),sQuery(id+"F0.wireOp",EDGE,"E35.filletArc"),sQuery(id+"F0.wireOp",EDGE,"E36.filletArc")])],"isStart":false}),makeQuery(id+"F7.opExtrude","SWEPT_FACE",FACE,{"disambiguationData":[OSD([sQuery(id+"F6.wireOp",EDGE,"E38")])]})]}),makeQuery(id+"F9.opExtrude","SWEPT_FACE",FACE,{"disambiguationData":[OSD([sQuery(id+"F8.wireOp",EDGE,"E51"),sQuery(id+"F8.wireOp",EDGE,"E52")])]})]}),makeQuery(id+"F22.opExtrude","SWEPT_FACE",FACE,{"disambiguationData":[OSD([sQuery(id+"F21.wireOp",EDGE,"E62")])]})]}),makeQuery(id+"F26.opExtrude","SWEPT_FACE",FACE,{"disambiguationData":[OSD([sQuery(id+"F25.wireOp",EDGE,"E67")])]})]});
            var sketch = newSketch(context, id + "F35", { "sketchPlane" : qUnion([Q0])});
            skArc(sketch, "E121", {"start": v(-33.75, 5.98) * mm, "mid": v(-32.78, 9.4) * mm, "end": v(-33.75, 12.83) * mm});
            skSolve(sketch);
        }
        {
            var Q0;
            {var subQ0=sQuery(id+"F35.wireOp",EDGE,"E121");Q0=makeQuery(id+"F35.imprint","IMPRINT",FACE,{"disambiguationData":[TD([[makeQuery(id+"F35.imprint","IMPRINT",EDGE,{"derivedFrom":subQ0}),1.0]])]});}
            extrude(context, id + "F36", {"entities" : qUnion([Q0]), "operationType" : NewBodyOperationType.REMOVE, "oppositeDirection" : true, "depth" : 50.8 * mm});
        }
        {
            var Q0;
            Q0=makeQuery(id+"F26.boolean.opBoolean","MERGE",FACE,{"derivedFrom":[makeQuery(id+"F22.boolean.opBoolean","MERGE",FACE,{"derivedFrom":[makeQuery(id+"F9.boolean.opBoolean","MERGE",FACE,{"derivedFrom":[makeQuery(id+"F7.boolean.opBoolean","MERGE",FACE,{"derivedFrom":[makeQuery(id+"F1.opExtrude","CAP_FACE",FACE,{"disambiguationData":[OSD([sQuery(id+"F0.wireOp",EDGE,"E0"),sQuery(id+"F0.wireOp",EDGE,"E1"),sQuery(id+"F0.wireOp",EDGE,"E2"),sQuery(id+"F0.wireOp",EDGE,"E3"),sQuery(id+"F0.wireOp",EDGE,"E4"),sQuery(id+"F0.wireOp",EDGE,"E5"),sQuery(id+"F0.wireOp",EDGE,"E6"),sQuery(id+"F0.wireOp",EDGE,"E7"),sQuery(id+"F0.wireOp",EDGE,"E8"),sQuery(id+"F0.wireOp",EDGE,"E9"),sQuery(id+"F0.wireOp",EDGE,"E10"),sQuery(id+"F0.wireOp",EDGE,"E11"),sQuery(id+"F0.wireOp",EDGE,"E12"),sQuery(id+"F0.wireOp",EDGE,"E13"),sQuery(id+"F0.wireOp",EDGE,"E14"),sQuery(id+"F0.wireOp",EDGE,"E15"),sQuery(id+"F0.wireOp",EDGE,"E18"),sQuery(id+"F0.wireOp",EDGE,"E20"),sQuery(id+"F0.wireOp",EDGE,"E25"),sQuery(id+"F0.wireOp",EDGE,"E26"),sQuery(id+"F0.wireOp",EDGE,"E27"),sQuery(id+"F0.wireOp",EDGE,"E28"),sQuery(id+"F0.wireOp",EDGE,"E29"),sQuery(id+"F0.wireOp",EDGE,"E30"),sQuery(id+"F0.wireOp",EDGE,"E31"),sQuery(id+"F0.wireOp",EDGE,"E32"),sQuery(id+"F0.wireOp",EDGE,"E33"),sQuery(id+"F0.wireOp",EDGE,"E34"),sQuery(id+"F0.wireOp",EDGE,"E35.filletArc"),sQuery(id+"F0.wireOp",EDGE,"E36.filletArc")])],"isStart":false}),makeQuery(id+"F7.opExtrude","SWEPT_FACE",FACE,{"disambiguationData":[OSD([sQuery(id+"F6.wireOp",EDGE,"E38")])]})]}),makeQuery(id+"F9.opExtrude","SWEPT_FACE",FACE,{"disambiguationData":[OSD([sQuery(id+"F8.wireOp",EDGE,"E51"),sQuery(id+"F8.wireOp",EDGE,"E52")])]})]}),makeQuery(id+"F22.opExtrude","SWEPT_FACE",FACE,{"disambiguationData":[OSD([sQuery(id+"F21.wireOp",EDGE,"E62")])]})]}),makeQuery(id+"F26.opExtrude","SWEPT_FACE",FACE,{"disambiguationData":[OSD([sQuery(id+"F25.wireOp",EDGE,"E67")])]})]});
            var sketch = newSketch(context, id + "F37", { "sketchPlane" : qUnion([Q0])});
            skLineSegment(sketch, "E122", {"start": v(56.87, 42.36) * mm, "end": v(81.45, 10.52) * mm});
            skLineSegment(sketch, "E123", {"start": v(81.45, 10.52) * mm, "end": v(78.57, 10.52) * mm});
            skLineSegment(sketch, "E124", {"start": v(78.57, 10.52) * mm, "end": v(55.44, 40.47) * mm});
            skLineSegment(sketch, "E125", {"start": v(55.44, 40.47) * mm, "end": v(56.87, 42.36) * mm});
            skSolve(sketch);
        }
        {
            var Q0;
            {var subQ0=sQuery(id+"F37.wireOp",EDGE,"E125");Q0=makeQuery(id+"F37.imprint","IMPRINT",FACE,{"disambiguationData":[TD([[makeQuery(id+"F37.imprint","IMPRINT",EDGE,{"derivedFrom":subQ0}),-1.0]])]});}
            var Q1;
            {var subQ0=sQuery(id+"F37.wireOp",EDGE,"E123");Q1=makeQuery(id+"F37.imprint","IMPRINT",FACE,{"disambiguationData":[TD([[makeQuery(id+"F37.imprint","IMPRINT",EDGE,{"derivedFrom":subQ0}),1.0]])]});}
            extrude(context, id + "F38", {"entities" : qUnion([Q0, Q1]), "operationType" : NewBodyOperationType.ADD, "oppositeDirection" : true, "depth" : 6.35 * mm, "hasSecondDirection" : true, "secondDirectionOppositeDirection" : true, "secondDirectionDepth" : 3.56 * mm});
        }
        {
            var Q0;
            {var subQ0=sQuery(id+"F37.wireOp",EDGE,"E125");Q0=makeQuery(id+"F37.imprint","IMPRINT",FACE,{"disambiguationData":[TD([[makeQuery(id+"F37.imprint","IMPRINT",EDGE,{"derivedFrom":subQ0}),-1.0]])]});}
            var Q1;
            {var subQ0=sQuery(id+"F37.wireOp",EDGE,"E123");Q1=makeQuery(id+"F37.imprint","IMPRINT",FACE,{"disambiguationData":[TD([[makeQuery(id+"F37.imprint","IMPRINT",EDGE,{"derivedFrom":subQ0}),1.0]])]});}
            extrude(context, id + "F39", {"entities" : qUnion([Q0, Q1]), "operationType" : NewBodyOperationType.ADD, "oppositeDirection" : true, "depth" : 47.27 * mm, "hasSecondDirection" : true, "secondDirectionOppositeDirection" : true, "secondDirectionDepth" : 44.45 * mm});
        }
        {
            var Q0;
            Q0=makeQuery(id+"F26.boolean.opBoolean","MERGE",FACE,{"derivedFrom":[makeQuery(id+"F22.boolean.opBoolean","MERGE",FACE,{"derivedFrom":[makeQuery(id+"F9.boolean.opBoolean","MERGE",FACE,{"derivedFrom":[makeQuery(id+"F7.boolean.opBoolean","MERGE",FACE,{"derivedFrom":[makeQuery(id+"F1.opExtrude","CAP_FACE",FACE,{"disambiguationData":[OSD([sQuery(id+"F0.wireOp",EDGE,"E0"),sQuery(id+"F0.wireOp",EDGE,"E1"),sQuery(id+"F0.wireOp",EDGE,"E2"),sQuery(id+"F0.wireOp",EDGE,"E3"),sQuery(id+"F0.wireOp",EDGE,"E4"),sQuery(id+"F0.wireOp",EDGE,"E5"),sQuery(id+"F0.wireOp",EDGE,"E6"),sQuery(id+"F0.wireOp",EDGE,"E7"),sQuery(id+"F0.wireOp",EDGE,"E8"),sQuery(id+"F0.wireOp",EDGE,"E9"),sQuery(id+"F0.wireOp",EDGE,"E10"),sQuery(id+"F0.wireOp",EDGE,"E11"),sQuery(id+"F0.wireOp",EDGE,"E12"),sQuery(id+"F0.wireOp",EDGE,"E13"),sQuery(id+"F0.wireOp",EDGE,"E14"),sQuery(id+"F0.wireOp",EDGE,"E15"),sQuery(id+"F0.wireOp",EDGE,"E18"),sQuery(id+"F0.wireOp",EDGE,"E20"),sQuery(id+"F0.wireOp",EDGE,"E25"),sQuery(id+"F0.wireOp",EDGE,"E26"),sQuery(id+"F0.wireOp",EDGE,"E27"),sQuery(id+"F0.wireOp",EDGE,"E28"),sQuery(id+"F0.wireOp",EDGE,"E29"),sQuery(id+"F0.wireOp",EDGE,"E30"),sQuery(id+"F0.wireOp",EDGE,"E31"),sQuery(id+"F0.wireOp",EDGE,"E32"),sQuery(id+"F0.wireOp",EDGE,"E33"),sQuery(id+"F0.wireOp",EDGE,"E34"),sQuery(id+"F0.wireOp",EDGE,"E35.filletArc"),sQuery(id+"F0.wireOp",EDGE,"E36.filletArc")])],"isStart":false}),makeQuery(id+"F7.opExtrude","SWEPT_FACE",FACE,{"disambiguationData":[OSD([sQuery(id+"F6.wireOp",EDGE,"E38")])]})]}),makeQuery(id+"F9.opExtrude","SWEPT_FACE",FACE,{"disambiguationData":[OSD([sQuery(id+"F8.wireOp",EDGE,"E51"),sQuery(id+"F8.wireOp",EDGE,"E52")])]})]}),makeQuery(id+"F22.opExtrude","SWEPT_FACE",FACE,{"disambiguationData":[OSD([sQuery(id+"F21.wireOp",EDGE,"E62")])]})]}),makeQuery(id+"F26.opExtrude","SWEPT_FACE",FACE,{"disambiguationData":[OSD([sQuery(id+"F25.wireOp",EDGE,"E67")])]})]});
            var sketch = newSketch(context, id + "F40", { "sketchPlane" : qUnion([Q0])});
            skLineSegment(sketch, "E126", {"start": v(23.77, 20.7) * mm, "end": v(22.7, 20.7) * mm});
            skLineSegment(sketch, "E127", {"start": v(22.7, 20.7) * mm, "end": v(22.7, 20.06) * mm});
            skLineSegment(sketch, "E128", {"start": v(22.7, 20.06) * mm, "end": v(23.77, 20.06) * mm});
            skLineSegment(sketch, "E129", {"start": v(23.77, 20.06) * mm, "end": v(23.77, 20.7) * mm});
            skLineSegment(sketch, "E130", {"start": v(20.42, 20.7) * mm, "end": v(20.42, 20.06) * mm});
            skLineSegment(sketch, "E131", {"start": v(20.42, 20.06) * mm, "end": v(19.35, 20.06) * mm});
            skLineSegment(sketch, "E132", {"start": v(19.35, 20.06) * mm, "end": v(19.35, 20.7) * mm});
            skLineSegment(sketch, "E133", {"start": v(19.35, 20.7) * mm, "end": v(20.42, 20.7) * mm});
            skSolve(sketch);
        }
        {
            var Q0;
            Q0=makeQuery(id+"F40.imprint","IMPRINT",FACE,{"disambiguationData":[TD([[makeQuery(id+"F40.imprint","IMPRINT",EDGE,{"derivedFrom":sQuery(id+"F40.wireOp",EDGE,"E126")}),1.0]])]});
            var Q1;
            Q1=makeQuery(id+"F40.imprint","IMPRINT",FACE,{"disambiguationData":[TD([[makeQuery(id+"F40.imprint","IMPRINT",EDGE,{"derivedFrom":sQuery(id+"F40.wireOp",EDGE,"E130")}),-1.0]])]});
            extrude(context, id + "F41", {"entities" : qUnion([Q0, Q1]), "operationType" : NewBodyOperationType.ADD, "depth" : 1.12 * mm});
        }
        {
            var Q0;
            Q0=makeQuery(id+"F40.imprint","IMPRINT",FACE,{"disambiguationData":[TD([[makeQuery(id+"F40.imprint","IMPRINT",EDGE,{"derivedFrom":sQuery(id+"F40.wireOp",EDGE,"E130")}),-1.0]])]});
            var Q1;
            Q1=makeQuery(id+"F40.imprint","IMPRINT",FACE,{"disambiguationData":[TD([[makeQuery(id+"F40.imprint","IMPRINT",EDGE,{"derivedFrom":sQuery(id+"F40.wireOp",EDGE,"E126")}),1.0]])]});
            extrude(context, id + "F42", {"entities" : qUnion([Q0, Q1]), "operationType" : NewBodyOperationType.ADD, "oppositeDirection" : true, "depth" : 51.92 * mm});
        }
        {
            var Q0;
            Q0=makeQuery(id+"F41.opExtrude","CAP_FACE",FACE,{"disambiguationData":[OSD([sQuery(id+"F40.wireOp",EDGE,"E126"),sQuery(id+"F40.wireOp",EDGE,"E127"),sQuery(id+"F40.wireOp",EDGE,"E128"),sQuery(id+"F40.wireOp",EDGE,"E129")])],"isStart":false});
            var sketch = newSketch(context, id + "F43", { "sketchPlane" : qUnion([Q0])});
            skLineSegment(sketch, "E134", {"start": v(23.77, 20.7) * mm, "end": v(19.36, 20.7) * mm});
            skPoint(sketch, "E134.endSnap0", {"position": v(23.24, 20.7) * mm});
            skLineSegment(sketch, "E135", {"start": v(19.36, 20.7) * mm, "end": v(19.36, 20.06) * mm});
            skLineSegment(sketch, "E136", {"start": v(19.36, 20.06) * mm, "end": v(23.77, 20.06) * mm});
            skLineSegment(sketch, "E137", {"start": v(23.77, 20.06) * mm, "end": v(23.77, 20.7) * mm});
            skSolve(sketch);
        }
        {
            var Q0;
            {var subQ0=sQuery(id+"F43.wireOp",EDGE,"E137");Q0=makeQuery(id+"F43.imprint","IMPRINT",FACE,{"disambiguationData":[TD([[makeQuery(id+"F43.imprint","IMPRINT",EDGE,{"derivedFrom":subQ0}),1.0]])]});}
            var Q1;
            {var subQ2=sQuery(id+"F43.wireOp",EDGE,"E135");Q1=makeQuery(id+"F43.imprint","IMPRINT",FACE,{"disambiguationData":[TD([[makeQuery(id+"F43.imprint","IMPRINT",EDGE,{"derivedFrom":subQ2}),1.0]])]});}
            extrude(context, id + "F44", {"entities" : qUnion([Q0, Q1]), "operationType" : NewBodyOperationType.ADD, "depth" : 0.64 * mm});
        }
        {
            var Q0;
            {var subQ2=sQuery(id+"F43.wireOp",EDGE,"E135");Q0=makeQuery(id+"F43.imprint","IMPRINT",FACE,{"disambiguationData":[TD([[makeQuery(id+"F43.imprint","IMPRINT",EDGE,{"derivedFrom":subQ2}),1.0]])]});}
            var Q1;
            {var subQ0=sQuery(id+"F43.wireOp",EDGE,"E137");Q1=makeQuery(id+"F43.imprint","IMPRINT",FACE,{"disambiguationData":[TD([[makeQuery(id+"F43.imprint","IMPRINT",EDGE,{"derivedFrom":subQ0}),1.0]])]});}
            extrude(context, id + "F45", {"entities" : qUnion([Q0, Q1]), "operationType" : NewBodyOperationType.ADD, "oppositeDirection" : true, "depth" : 53.62 * mm, "hasSecondDirection" : true, "secondDirectionOppositeDirection" : true, "secondDirectionDepth" : 52.96 * mm});
        }
        {
            var Q0;
            Q0=makeQuery(id+"F18.opExtrude","CAP_FACE",FACE,{"disambiguationData":[OSD([sQuery(id+"F0.wireOp",EDGE,"E27"),sQuery(id+"F0.wireOp",EDGE,"E28"),sQuery(id+"F0.wireOp",EDGE,"E29"),sQuery(id+"F0.wireOp",EDGE,"E30")])],"isStart":false});
            var sketch = newSketch(context, id + "F46", { "sketchPlane" : qUnion([Q0])});
            skLineSegment(sketch, "E138", {"start": v(12.77, 42.65) * mm, "end": v(12.77, 29.17) * mm});
            skLineSegment(sketch, "E139", {"start": v(12.77, 29.17) * mm, "end": v(11.98, 29.17) * mm});
            skLineSegment(sketch, "E140", {"start": v(11.98, 29.17) * mm, "end": v(11.98, 41.46) * mm});
            skLineSegment(sketch, "E141", {"start": v(11.98, 41.46) * mm, "end": v(12.77, 42.65) * mm});
            skSolve(sketch);
        }
        {
            var Q0;
            Q0=makeQuery(id+"F46.imprint","IMPRINT",FACE,{"disambiguationData":[TD([[makeQuery(id+"F46.imprint","IMPRINT",EDGE,{"derivedFrom":sQuery(id+"F46.wireOp",EDGE,"E138")}),-1.0]])]});
            extrude(context, id + "F47", {"entities" : qUnion([Q0]), "operationType" : NewBodyOperationType.ADD, "depth" : 0.76 * mm});
        }
        {
            var Q0;
            Q0=makeQuery(id+"F46.imprint","IMPRINT",FACE,{"disambiguationData":[TD([[makeQuery(id+"F46.imprint","IMPRINT",EDGE,{"derivedFrom":sQuery(id+"F46.wireOp",EDGE,"E138")}),-1.0]])]});
            extrude(context, id + "F48", {"entities" : qUnion([Q0]), "operationType" : NewBodyOperationType.ADD, "oppositeDirection" : true, "depth" : 49 * mm});
        }
        {
            var Q0;
            Q0=makeQuery(id+"F26.boolean.opBoolean","MERGE",FACE,{"derivedFrom":[makeQuery(id+"F22.boolean.opBoolean","MERGE",FACE,{"derivedFrom":[makeQuery(id+"F9.boolean.opBoolean","MERGE",FACE,{"derivedFrom":[makeQuery(id+"F7.boolean.opBoolean","MERGE",FACE,{"derivedFrom":[makeQuery(id+"F2.opExtrude","CAP_FACE",FACE,{"disambiguationData":[OSD([sQuery(id+"F0.wireOp",EDGE,"E0"),sQuery(id+"F0.wireOp",EDGE,"E1"),sQuery(id+"F0.wireOp",EDGE,"E2"),sQuery(id+"F0.wireOp",EDGE,"E3"),sQuery(id+"F0.wireOp",EDGE,"E4"),sQuery(id+"F0.wireOp",EDGE,"E5"),sQuery(id+"F0.wireOp",EDGE,"E6"),sQuery(id+"F0.wireOp",EDGE,"E7"),sQuery(id+"F0.wireOp",EDGE,"E8"),sQuery(id+"F0.wireOp",EDGE,"E9"),sQuery(id+"F0.wireOp",EDGE,"E10"),sQuery(id+"F0.wireOp",EDGE,"E11"),sQuery(id+"F0.wireOp",EDGE,"E12"),sQuery(id+"F0.wireOp",EDGE,"E13"),sQuery(id+"F0.wireOp",EDGE,"E14"),sQuery(id+"F0.wireOp",EDGE,"E15"),sQuery(id+"F0.wireOp",EDGE,"E18"),sQuery(id+"F0.wireOp",EDGE,"E20"),sQuery(id+"F0.wireOp",EDGE,"E25"),sQuery(id+"F0.wireOp",EDGE,"E26"),sQuery(id+"F0.wireOp",EDGE,"E27"),sQuery(id+"F0.wireOp",EDGE,"E28"),sQuery(id+"F0.wireOp",EDGE,"E29"),sQuery(id+"F0.wireOp",EDGE,"E30"),sQuery(id+"F0.wireOp",EDGE,"E31"),sQuery(id+"F0.wireOp",EDGE,"E32"),sQuery(id+"F0.wireOp",EDGE,"E33"),sQuery(id+"F0.wireOp",EDGE,"E34"),sQuery(id+"F0.wireOp",EDGE,"E35.filletArc"),sQuery(id+"F0.wireOp",EDGE,"E36.filletArc")])],"isStart":false}),makeQuery(id+"F7.opExtrude","SWEPT_FACE",FACE,{"disambiguationData":[OSD([sQuery(id+"F6.wireOp",EDGE,"E40")])]})]}),makeQuery(id+"F9.opExtrude","SWEPT_FACE",FACE,{"disambiguationData":[OSD([sQuery(id+"F8.wireOp",EDGE,"E44"),sQuery(id+"F8.wireOp",EDGE,"E45")])]})]}),makeQuery(id+"F22.opExtrude","SWEPT_FACE",FACE,{"disambiguationData":[OSD([sQuery(id+"F21.wireOp",EDGE,"E60")])]})]}),makeQuery(id+"F26.opExtrude","SWEPT_FACE",FACE,{"disambiguationData":[OSD([sQuery(id+"F25.wireOp",EDGE,"E74")])]})]});
            var sketch = newSketch(context, id + "F49", { "sketchPlane" : qUnion([Q0])});
            skLineSegment(sketch, "E142", {"start": v(-6.88, 28.14) * mm, "end": v(-8.5, 28.14) * mm});
            skLineSegment(sketch, "E143", {"start": v(-8.5, 28.14) * mm, "end": v(-8, 26.34) * mm});
            skLineSegment(sketch, "E144", {"start": v(-8, 26.34) * mm, "end": v(-7.35, 26.34) * mm});
            skLineSegment(sketch, "E145", {"start": v(-7.35, 26.34) * mm, "end": v(-6.88, 28.14) * mm});
            skSolve(sketch);
        }
        {
            var Q0;
            Q0=makeQuery(id+"F49.imprint","IMPRINT",FACE,{"disambiguationData":[TD([[makeQuery(id+"F49.imprint","IMPRINT",EDGE,{"derivedFrom":sQuery(id+"F49.wireOp",EDGE,"E142")}),1.0]])]});
            extrude(context, id + "F50", {"entities" : qUnion([Q0]), "operationType" : NewBodyOperationType.ADD, "depth" : 0.5 * mm});
        }
        {
            var Q0;
            Q0=makeQuery(id+"F50.opExtrude","CAP_EDGE",EDGE,{"disambiguationData":[OSD([sQuery(id+"F49.wireOp",EDGE,"E145")])],"isStart":false});
            var Q1;
            Q1=makeQuery(id+"F50.opExtrude","CAP_EDGE",EDGE,{"disambiguationData":[OSD([sQuery(id+"F49.wireOp",EDGE,"E143")])],"isStart":false});
            var Q2;
            Q2=makeQuery(id+"F50.opExtrude","CAP_EDGE",EDGE,{"disambiguationData":[OSD([sQuery(id+"F49.wireOp",EDGE,"E144")])],"isStart":false});
            fillet(context, id + "F51", {"entities" : qUnion([Q0, Q1, Q2]), "radius" : 0.25 * mm, "tangentPropagation" : true, "allowEdgeOverflow" : false});
        }
        {
            var Q0;
            Q0=makeQuery(id+"F49.imprint","IMPRINT",FACE,{"disambiguationData":[TD([[makeQuery(id+"F49.imprint","IMPRINT",EDGE,{"derivedFrom":sQuery(id+"F49.wireOp",EDGE,"E142")}),1.0]])]});
            extrude(context, id + "F52", {"entities" : qUnion([Q0]), "operationType" : NewBodyOperationType.ADD, "oppositeDirection" : true, "depth" : 51.3 * mm});
        }
        {
            var Q0;
            Q0=makeQuery(id+"F52.opExtrude","CAP_EDGE",EDGE,{"disambiguationData":[OSD([sQuery(id+"F49.wireOp",EDGE,"E143")])],"isStart":false});
            var Q1;
            Q1=makeQuery(id+"F52.opExtrude","CAP_EDGE",EDGE,{"disambiguationData":[OSD([sQuery(id+"F49.wireOp",EDGE,"E145")])],"isStart":false});
            var Q2;
            Q2=makeQuery(id+"F52.opExtrude","CAP_EDGE",EDGE,{"disambiguationData":[OSD([sQuery(id+"F49.wireOp",EDGE,"E144")])],"isStart":false});
            fillet(context, id + "F53", {"entities" : qUnion([Q0, Q1, Q2]), "radius" : 0.25 * mm, "tangentPropagation" : true, "allowEdgeOverflow" : false});
        }
        {
            var Q0;
            Q0=makeQuery(id+"F52.opExtrude","SWEPT_FACE",FACE,{"disambiguationData":[OSD([sQuery(id+"F49.wireOp",EDGE,"E142")])]});
            var sketch = newSketch(context, id + "F54", { "sketchPlane" : qUnion([Q0])});
            skLineSegment(sketch, "E146", {"start": v(7.98, -25.4) * mm, "end": v(7.98, -25.9) * mm});
            skPoint(sketch, "E146.startSnap0", {"position": v(7.98, -25.65) * mm});
            skPoint(sketch, "E146.endSnap0", {"position": v(7.98, -25.65) * mm});
            skLineSegment(sketch, "E147", {"start": v(7.98, -25.9) * mm, "end": v(7.47, -25.9) * mm});
            skLineSegment(sketch, "E148", {"start": v(7.47, -25.9) * mm, "end": v(7.47, -25.4) * mm});
            skLineSegment(sketch, "E149", {"start": v(7.47, -25.4) * mm, "end": v(7.98, -25.4) * mm});
            skSolve(sketch);
        }
        {
            var Q0;
            Q0=makeQuery(id+"F54.imprint","IMPRINT",FACE,{"disambiguationData":[TD([[makeQuery(id+"F54.imprint","IMPRINT",EDGE,{"derivedFrom":sQuery(id+"F54.wireOp",EDGE,"E146")}),-1.0]])]});
            extrude(context, id + "F55", {"entities" : qUnion([Q0]), "operationType" : NewBodyOperationType.ADD, "depth" : 2.54 * mm});
        }
        {
            var Q0;
            Q0=makeQuery(id+"F50.opExtrude","SWEPT_FACE",FACE,{"disambiguationData":[OSD([sQuery(id+"F49.wireOp",EDGE,"E142")])]});
            var sketch = newSketch(context, id + "F56", { "sketchPlane" : qUnion([Q0])});
            skLineSegment(sketch, "E150", {"start": v(7.35, 25.4) * mm, "end": v(7.35, 25.9) * mm});
            skLineSegment(sketch, "E151", {"start": v(7.35, 25.9) * mm, "end": v(7.85, 25.9) * mm});
            skLineSegment(sketch, "E152", {"start": v(7.85, 25.9) * mm, "end": v(7.85, 25.4) * mm});
            skLineSegment(sketch, "E153", {"start": v(7.85, 25.4) * mm, "end": v(7.35, 25.4) * mm});
            skSolve(sketch);
        }
        {
            var Q0;
            Q0=makeQuery(id+"F56.imprint","IMPRINT",FACE,{"disambiguationData":[TD([[makeQuery(id+"F56.imprint","IMPRINT",EDGE,{"derivedFrom":sQuery(id+"F56.wireOp",EDGE,"E150")}),-1.0]])]});
            extrude(context, id + "F57", {"entities" : qUnion([Q0]), "operationType" : NewBodyOperationType.ADD, "depth" : 2.54 * mm});
        }
        {
            var Q0;
            Q0=makeQuery(id+"F57.boolean.opBoolean","MERGE",FACE,{"derivedFrom":[makeQuery(id+"F50.opExtrude","CAP_FACE",FACE,{"disambiguationData":[OSD([sQuery(id+"F49.wireOp",EDGE,"E142"),sQuery(id+"F49.wireOp",EDGE,"E143"),sQuery(id+"F49.wireOp",EDGE,"E144"),sQuery(id+"F49.wireOp",EDGE,"E145")])],"isStart":false}),makeQuery(id+"F57.opExtrude","SWEPT_FACE",FACE,{"disambiguationData":[OSD([sQuery(id+"F56.wireOp",EDGE,"E151")])]})]});
            var sketch = newSketch(context, id + "F58", { "sketchPlane" : qUnion([Q0])});
            skLineSegment(sketch, "E154", {"start": v(-7.35, 30.68) * mm, "end": v(-7.35, 30.17) * mm});
            skLineSegment(sketch, "E155", {"start": v(-7.35, 30.17) * mm, "end": v(-7.85, 30.17) * mm});
            skLineSegment(sketch, "E156", {"start": v(-7.85, 30.17) * mm, "end": v(-7.85, 30.68) * mm});
            skLineSegment(sketch, "E157", {"start": v(-7.85, 30.68) * mm, "end": v(-7.35, 30.68) * mm});
            skSolve(sketch);
        }
        {
            var Q0;
            Q0=makeQuery(id+"F58.imprint","IMPRINT",FACE,{"disambiguationData":[TD([[makeQuery(id+"F58.imprint","IMPRINT",EDGE,{"derivedFrom":sQuery(id+"F58.wireOp",EDGE,"E154")}),-1.0]])]});
            extrude(context, id + "F59", {"entities" : qUnion([Q0]), "operationType" : NewBodyOperationType.ADD, "depth" : 2.54 * mm});
        }
        {
            var Q0;
            Q0=makeQuery(id+"F55.boolean.opBoolean","MERGE",FACE,{"derivedFrom":[makeQuery(id+"F52.opExtrude","CAP_FACE",FACE,{"disambiguationData":[OSD([sQuery(id+"F49.wireOp",EDGE,"E142"),sQuery(id+"F49.wireOp",EDGE,"E143"),sQuery(id+"F49.wireOp",EDGE,"E144"),sQuery(id+"F49.wireOp",EDGE,"E145")])],"isStart":false}),makeQuery(id+"F55.opExtrude","SWEPT_FACE",FACE,{"disambiguationData":[OSD([sQuery(id+"F54.wireOp",EDGE,"E147")])]})]});
            var sketch = newSketch(context, id + "F60", { "sketchPlane" : qUnion([Q0])});
            skLineSegment(sketch, "E158", {"start": v(7.98, 30.68) * mm, "end": v(7.98, 30.17) * mm});
            skLineSegment(sketch, "E159", {"start": v(7.98, 30.17) * mm, "end": v(7.47, 30.17) * mm});
            skLineSegment(sketch, "E160", {"start": v(7.47, 30.17) * mm, "end": v(7.47, 30.68) * mm});
            skLineSegment(sketch, "E161", {"start": v(7.47, 30.68) * mm, "end": v(7.98, 30.68) * mm});
            skSolve(sketch);
        }
        {
            var Q0;
            Q0=makeQuery(id+"F60.imprint","IMPRINT",FACE,{"disambiguationData":[TD([[makeQuery(id+"F60.imprint","IMPRINT",EDGE,{"derivedFrom":sQuery(id+"F60.wireOp",EDGE,"E158")}),-1.0]])]});
            extrude(context, id + "F61", {"entities" : qUnion([Q0]), "operationType" : NewBodyOperationType.ADD, "depth" : 2.54 * mm});
        }
        {
            var Q0;
            Q0=makeQuery(id+"F55.opExtrude","CAP_EDGE",EDGE,{"disambiguationData":[OSD([sQuery(id+"F54.wireOp",EDGE,"E149")])],"isStart":false});
            var Q1;
            Q1=makeQuery(id+"F57.opExtrude","CAP_EDGE",EDGE,{"disambiguationData":[OSD([sQuery(id+"F56.wireOp",EDGE,"E153")])],"isStart":false});
            fillet(context, id + "F62", {"entities" : qUnion([Q0, Q1]), "radius" : 0.25 * mm, "tangentPropagation" : true, "allowEdgeOverflow" : false});
        }
        {
            var Q0;
            Q0=makeQuery(id+"F59.opExtrude","CAP_FACE",FACE,{"disambiguationData":[OSD([sQuery(id+"F58.wireOp",EDGE,"E154"),sQuery(id+"F58.wireOp",EDGE,"E155"),sQuery(id+"F58.wireOp",EDGE,"E156"),sQuery(id+"F58.wireOp",EDGE,"E157")])],"isStart":false});
            var sketch = newSketch(context, id + "F63", { "sketchPlane" : qUnion([Q0])});
            skLineSegment(sketch, "E162", {"start": v(-7.35, 31.46) * mm, "end": v(-7.35, 29.42) * mm});
            skLineSegment(sketch, "E163", {"start": v(-7.35, 29.42) * mm, "end": v(-7.94, 29.42) * mm});
            skLineSegment(sketch, "E164", {"start": v(-7.94, 29.42) * mm, "end": v(-7.94, 31.46) * mm});
            skLineSegment(sketch, "E165", {"start": v(-7.94, 31.46) * mm, "end": v(-7.35, 31.46) * mm});
            skSolve(sketch);
        }
        {
            var Q0;
            {var subQ0=sQuery(id+"F63.wireOp",EDGE,"E163");Q0=makeQuery(id+"F63.imprint","IMPRINT",FACE,{"disambiguationData":[TD([[makeQuery(id+"F63.imprint","IMPRINT",EDGE,{"derivedFrom":subQ0}),-1.0]])]});}
            var Q1;
            {var subQ2=makeQuery(id+"F59.opExtrude","CAP_EDGE",EDGE,{"disambiguationData":[OSD([sQuery(id+"F58.wireOp",EDGE,"E155")])],"isStart":false});Q1=makeQuery(id+"F63.imprint","IMPRINT",FACE,{"disambiguationData":[TD([[makeQuery(id+"F63.imprint","IMPRINT",EDGE,{"derivedFrom":subQ2}),-1.0]])]});}
            extrude(context, id + "F64", {"entities" : qUnion([Q0, Q1]), "operationType" : NewBodyOperationType.ADD, "depth" : 2.54 * mm});
        }
        {
            var Q0;
            Q0=makeQuery(id+"F64.opExtrude","CAP_EDGE",EDGE,{"disambiguationData":[OSD([sQuery(id+"F63.wireOp",EDGE,"E164")])],"isStart":false});
            var Q1;
            Q1=makeQuery(id+"F64.opExtrude","SWEPT_EDGE",EDGE,{"disambiguationData":[OSD([sQuery(id+"F63.wireOp",EDGE,"E164"),sQuery(id+"F63.wireOp",EDGE,"E165")])]});
            var Q2;
            Q2=makeQuery(id+"F64.opExtrude","SWEPT_EDGE",EDGE,{"disambiguationData":[OSD([sQuery(id+"F63.wireOp",EDGE,"E163"),sQuery(id+"F63.wireOp",EDGE,"E164")])]});
            var Q3;
            Q3=makeQuery(id+"F64.opExtrude","CAP_EDGE",EDGE,{"disambiguationData":[OSD([sQuery(id+"F63.wireOp",EDGE,"E162")])],"isStart":false});
            var Q4;
            Q4=makeQuery(id+"F64.opExtrude","SWEPT_EDGE",EDGE,{"disambiguationData":[OSD([sQuery(id+"F63.wireOp",EDGE,"E162"),sQuery(id+"F63.wireOp",EDGE,"E165")])]});
            var Q5;
            Q5=makeQuery(id+"F64.opExtrude","CAP_EDGE",EDGE,{"disambiguationData":[OSD([sQuery(id+"F63.wireOp",EDGE,"E164")])],"isStart":true});
            fillet(context, id + "F65", {"entities" : qUnion([Q0, Q1, Q2, Q3, Q4, Q5]), "radius" : 0.25 * mm, "tangentPropagation" : true, "allowEdgeOverflow" : false});
        }
        {
            var Q0;
            Q0=makeQuery(id+"F61.opExtrude","CAP_FACE",FACE,{"disambiguationData":[OSD([sQuery(id+"F60.wireOp",EDGE,"E158"),sQuery(id+"F60.wireOp",EDGE,"E159"),sQuery(id+"F60.wireOp",EDGE,"E160"),sQuery(id+"F60.wireOp",EDGE,"E161")])],"isStart":false});
            var sketch = newSketch(context, id + "F66", { "sketchPlane" : qUnion([Q0])});
            skLineSegment(sketch, "E166", {"start": v(7.45, 31.3) * mm, "end": v(7.47, 29.27) * mm});
            skLineSegment(sketch, "E167", {"start": v(7.47, 29.27) * mm, "end": v(8.1, 29.27) * mm});
            skLineSegment(sketch, "E168", {"start": v(8.1, 29.27) * mm, "end": v(8.1, 31.3) * mm});
            skLineSegment(sketch, "E169", {"start": v(8.1, 31.3) * mm, "end": v(7.45, 31.3) * mm});
            skSolve(sketch);
        }
        {
            var Q0;
            Q0=makeQuery(id+"F66.imprint","IMPRINT",FACE,{"disambiguationData":[TD([[makeQuery(id+"F66.imprint","IMPRINT",EDGE,{"derivedFrom":makeQuery(id+"F61.opExtrude","CAP_EDGE",EDGE,{"disambiguationData":[OSD([sQuery(id+"F60.wireOp",EDGE,"E158")])],"isStart":false})}),-1.0]])]});
            var Q1;
            Q1=makeQuery(id+"F66.imprint","IMPRINT",FACE,{"disambiguationData":[TD([[makeQuery(id+"F66.imprint","IMPRINT",EDGE,{"derivedFrom":sQuery(id+"F66.wireOp",EDGE,"E166")}),1.0]])]});
            extrude(context, id + "F67", {"entities" : qUnion([Q0, Q1]), "operationType" : NewBodyOperationType.ADD, "depth" : 2.54 * mm});
        }
        {
            var Q0;
            Q0=makeQuery(id+"F67.opExtrude","SWEPT_EDGE",EDGE,{"disambiguationData":[OSD([sQuery(id+"F66.wireOp",EDGE,"E168"),sQuery(id+"F66.wireOp",EDGE,"E169")])]});
            var Q1;
            Q1=makeQuery(id+"F67.opExtrude","CAP_EDGE",EDGE,{"disambiguationData":[OSD([sQuery(id+"F66.wireOp",EDGE,"E168")])],"isStart":false});
            var Q2;
            Q2=makeQuery(id+"F67.opExtrude","SWEPT_EDGE",EDGE,{"disambiguationData":[OSD([sQuery(id+"F66.wireOp",EDGE,"E167"),sQuery(id+"F66.wireOp",EDGE,"E168")])]});
            var Q3;
            Q3=makeQuery(id+"F67.opExtrude","CAP_EDGE",EDGE,{"disambiguationData":[OSD([sQuery(id+"F66.wireOp",EDGE,"E168")])],"isStart":true});
            var Q4;
            Q4=makeQuery(id+"F67.opExtrude","CAP_EDGE",EDGE,{"disambiguationData":[OSD([sQuery(id+"F66.wireOp",EDGE,"E166")])],"isStart":false});
            var Q5;
            Q5=makeQuery(id+"F67.opExtrude","SWEPT_EDGE",EDGE,{"disambiguationData":[OSD([sQuery(id+"F66.wireOp",EDGE,"E166"),sQuery(id+"F66.wireOp",EDGE,"E169")])]});
            fillet(context, id + "F68", {"entities" : qUnion([Q0, Q1, Q2, Q3, Q4, Q5]), "radius" : 0.25 * mm, "tangentPropagation" : true, "allowEdgeOverflow" : false});
        }
        {
            var Q0;
            {var subQ0=sQuery(id+"F0.wireOp",EDGE,"E23");Q0=makeQuery(id+"F14.boolean.opBoolean","MERGE",FACE,{"derivedFrom":[makeQuery(id+"F13.opExtrude","SWEPT_FACE",FACE,{"disambiguationData":[OSD([subQ0])]}),makeQuery(id+"F14.opExtrude","SWEPT_FACE",FACE,{"disambiguationData":[OSD([subQ0])]})]});}
            var sketch = newSketch(context, id + "F69", { "sketchPlane" : qUnion([Q0])});
            skLineSegment(sketch, "E170", {"start": v(3.51, 0) * mm, "end": v(-3.35, 0) * mm});
            skLineSegment(sketch, "E171", {"start": v(-3.35, 0) * mm, "end": v(-3.35, -2.3) * mm});
            skLineSegment(sketch, "E172", {"start": v(-3.35, -2.3) * mm, "end": v(3.51, -2.3) * mm});
            skLineSegment(sketch, "E173", {"start": v(3.51, -2.3) * mm, "end": v(3.51, 0) * mm});
            skSolve(sketch);
        }
        {
            var Q0;
            Q0=makeQuery(id+"F69.imprint","IMPRINT",FACE,{"disambiguationData":[TD([[makeQuery(id+"F69.imprint","IMPRINT",EDGE,{"derivedFrom":sQuery(id+"F69.wireOp",EDGE,"E170")}),1.0]])]});
            extrude(context, id + "F70", {"entities" : qUnion([Q0]), "operationType" : NewBodyOperationType.ADD, "oppositeDirection" : true, "depth" : 0.25 * mm});
        }
        {
            var Q0;
            Q0=makeQuery(id+"F26.boolean.opBoolean","MERGE",FACE,{"derivedFrom":[makeQuery(id+"F22.boolean.opBoolean","MERGE",FACE,{"derivedFrom":[makeQuery(id+"F9.boolean.opBoolean","MERGE",FACE,{"derivedFrom":[makeQuery(id+"F7.boolean.opBoolean","MERGE",FACE,{"derivedFrom":[makeQuery(id+"F2.opExtrude","CAP_FACE",FACE,{"disambiguationData":[OSD([sQuery(id+"F0.wireOp",EDGE,"E0"),sQuery(id+"F0.wireOp",EDGE,"E1"),sQuery(id+"F0.wireOp",EDGE,"E2"),sQuery(id+"F0.wireOp",EDGE,"E3"),sQuery(id+"F0.wireOp",EDGE,"E4"),sQuery(id+"F0.wireOp",EDGE,"E5"),sQuery(id+"F0.wireOp",EDGE,"E6"),sQuery(id+"F0.wireOp",EDGE,"E7"),sQuery(id+"F0.wireOp",EDGE,"E8"),sQuery(id+"F0.wireOp",EDGE,"E9"),sQuery(id+"F0.wireOp",EDGE,"E10"),sQuery(id+"F0.wireOp",EDGE,"E11"),sQuery(id+"F0.wireOp",EDGE,"E12"),sQuery(id+"F0.wireOp",EDGE,"E13"),sQuery(id+"F0.wireOp",EDGE,"E14"),sQuery(id+"F0.wireOp",EDGE,"E15"),sQuery(id+"F0.wireOp",EDGE,"E18"),sQuery(id+"F0.wireOp",EDGE,"E20"),sQuery(id+"F0.wireOp",EDGE,"E25"),sQuery(id+"F0.wireOp",EDGE,"E26"),sQuery(id+"F0.wireOp",EDGE,"E27"),sQuery(id+"F0.wireOp",EDGE,"E28"),sQuery(id+"F0.wireOp",EDGE,"E29"),sQuery(id+"F0.wireOp",EDGE,"E30"),sQuery(id+"F0.wireOp",EDGE,"E31"),sQuery(id+"F0.wireOp",EDGE,"E32"),sQuery(id+"F0.wireOp",EDGE,"E33"),sQuery(id+"F0.wireOp",EDGE,"E34"),sQuery(id+"F0.wireOp",EDGE,"E35.filletArc"),sQuery(id+"F0.wireOp",EDGE,"E36.filletArc")])],"isStart":false}),makeQuery(id+"F7.opExtrude","SWEPT_FACE",FACE,{"disambiguationData":[OSD([sQuery(id+"F6.wireOp",EDGE,"E40")])]})]}),makeQuery(id+"F9.opExtrude","SWEPT_FACE",FACE,{"disambiguationData":[OSD([sQuery(id+"F8.wireOp",EDGE,"E44"),sQuery(id+"F8.wireOp",EDGE,"E45")])]})]}),makeQuery(id+"F22.opExtrude","SWEPT_FACE",FACE,{"disambiguationData":[OSD([sQuery(id+"F21.wireOp",EDGE,"E60")])]})]}),makeQuery(id+"F26.opExtrude","SWEPT_FACE",FACE,{"disambiguationData":[OSD([sQuery(id+"F25.wireOp",EDGE,"E74")])]})]});
            var sketch = newSketch(context, id + "F71", { "sketchPlane" : qUnion([Q0])});
            skLineSegment(sketch, "E174", {"start": v(25.94, 9.85) * mm, "end": v(25.94, 8.42) * mm});
            skLineSegment(sketch, "E175", {"start": v(30.86, 9.85) * mm, "end": v(30.86, 8.42) * mm});
            skLineSegment(sketch, "E176", {"start": v(30.86, 9.85) * mm, "end": v(25.94, 9.85) * mm});
            skLineSegment(sketch, "E177", {"start": v(25.94, 8.42) * mm, "end": v(30.86, 8.42) * mm});
            skSolve(sketch);
        }
        {
            var Q0;
            Q0=makeQuery(id+"F71.imprint","IMPRINT",FACE,{"disambiguationData":[TD([[makeQuery(id+"F71.imprint","IMPRINT",EDGE,{"derivedFrom":sQuery(id+"F71.wireOp",EDGE,"E174")}),1.0]])]});
            extrude(context, id + "F72", {"entities" : qUnion([Q0]), "operationType" : NewBodyOperationType.ADD, "depth" : 0.25 * mm});
        }
        {
            var Q0;
            Q0=makeQuery(id+"F26.boolean.opBoolean","MERGE",FACE,{"derivedFrom":[makeQuery(id+"F22.boolean.opBoolean","MERGE",FACE,{"derivedFrom":[makeQuery(id+"F9.boolean.opBoolean","MERGE",FACE,{"derivedFrom":[makeQuery(id+"F7.boolean.opBoolean","MERGE",FACE,{"derivedFrom":[makeQuery(id+"F2.opExtrude","CAP_FACE",FACE,{"disambiguationData":[OSD([sQuery(id+"F0.wireOp",EDGE,"E0"),sQuery(id+"F0.wireOp",EDGE,"E1"),sQuery(id+"F0.wireOp",EDGE,"E2"),sQuery(id+"F0.wireOp",EDGE,"E3"),sQuery(id+"F0.wireOp",EDGE,"E4"),sQuery(id+"F0.wireOp",EDGE,"E5"),sQuery(id+"F0.wireOp",EDGE,"E6"),sQuery(id+"F0.wireOp",EDGE,"E7"),sQuery(id+"F0.wireOp",EDGE,"E8"),sQuery(id+"F0.wireOp",EDGE,"E9"),sQuery(id+"F0.wireOp",EDGE,"E10"),sQuery(id+"F0.wireOp",EDGE,"E11"),sQuery(id+"F0.wireOp",EDGE,"E12"),sQuery(id+"F0.wireOp",EDGE,"E13"),sQuery(id+"F0.wireOp",EDGE,"E14"),sQuery(id+"F0.wireOp",EDGE,"E15"),sQuery(id+"F0.wireOp",EDGE,"E18"),sQuery(id+"F0.wireOp",EDGE,"E20"),sQuery(id+"F0.wireOp",EDGE,"E25"),sQuery(id+"F0.wireOp",EDGE,"E26"),sQuery(id+"F0.wireOp",EDGE,"E27"),sQuery(id+"F0.wireOp",EDGE,"E28"),sQuery(id+"F0.wireOp",EDGE,"E29"),sQuery(id+"F0.wireOp",EDGE,"E30"),sQuery(id+"F0.wireOp",EDGE,"E31"),sQuery(id+"F0.wireOp",EDGE,"E32"),sQuery(id+"F0.wireOp",EDGE,"E33"),sQuery(id+"F0.wireOp",EDGE,"E34"),sQuery(id+"F0.wireOp",EDGE,"E35.filletArc"),sQuery(id+"F0.wireOp",EDGE,"E36.filletArc")])],"isStart":false}),makeQuery(id+"F7.opExtrude","SWEPT_FACE",FACE,{"disambiguationData":[OSD([sQuery(id+"F6.wireOp",EDGE,"E40")])]})]}),makeQuery(id+"F9.opExtrude","SWEPT_FACE",FACE,{"disambiguationData":[OSD([sQuery(id+"F8.wireOp",EDGE,"E44"),sQuery(id+"F8.wireOp",EDGE,"E45")])]})]}),makeQuery(id+"F22.opExtrude","SWEPT_FACE",FACE,{"disambiguationData":[OSD([sQuery(id+"F21.wireOp",EDGE,"E60")])]})]}),makeQuery(id+"F26.opExtrude","SWEPT_FACE",FACE,{"disambiguationData":[OSD([sQuery(id+"F25.wireOp",EDGE,"E74")])]})]});
            var sketch = newSketch(context, id + "F73", { "sketchPlane" : qUnion([Q0])});
            skLineSegment(sketch, "E178", {"start": v(30.86, 9.85) * mm, "end": v(25.94, 9.85) * mm});
            skLineSegment(sketch, "E179", {"start": v(25.94, 9.85) * mm, "end": v(25.94, 8.42) * mm});
            skLineSegment(sketch, "E180", {"start": v(25.94, 8.42) * mm, "end": v(30.86, 8.42) * mm});
            skSolve(sketch);
        }
        {
            var Q0;
            Q0=makeQuery(id+"F72.opExtrude","CAP_FACE",FACE,{"disambiguationData":[OSD([sQuery(id+"F71.wireOp",EDGE,"E174"),sQuery(id+"F71.wireOp",EDGE,"E175"),sQuery(id+"F71.wireOp",EDGE,"E176"),sQuery(id+"F71.wireOp",EDGE,"E177")])],"isStart":false});
            extrude(context, id + "F74", {"entities" : qUnion([Q0]), "operationType" : NewBodyOperationType.ADD, "oppositeDirection" : true, "depth" : 51.3 * mm});
        }
        {
            var Q0;
            {var subQ0=sQuery(id+"F0.wireOp",EDGE,"E8");Q0=makeQuery(id+"F2.boolean.opBoolean","MERGE",FACE,{"derivedFrom":[makeQuery(id+"F1.opExtrude","SWEPT_FACE",FACE,{"disambiguationData":[OSD([subQ0])]}),makeQuery(id+"F2.opExtrude","SWEPT_FACE",FACE,{"disambiguationData":[OSD([subQ0])]})]});}
            var sketch = newSketch(context, id + "F75", { "sketchPlane" : qUnion([Q0])});
            skLineSegment(sketch, "E181", {"start": v(-22.68, 23.47) * mm, "end": v(-23.32, 23.7) * mm});
            skLineSegment(sketch, "E182", {"start": v(-23.32, 23.7) * mm, "end": v(-23.32, 23.84) * mm});
            skLineSegment(sketch, "E183", {"start": v(-23.32, 23.84) * mm, "end": v(-22.68, 24.04) * mm});
            skLineSegment(sketch, "E184", {"start": v(-22.68, 24.04) * mm, "end": v(-9.22, 24.04) * mm});
            skLineSegment(sketch, "E185", {"start": v(-9.22, 24.04) * mm, "end": v(-9.22, 23.47) * mm});
            skLineSegment(sketch, "E186", {"start": v(-9.22, 23.47) * mm, "end": v(-22.68, 23.47) * mm});
            skLineSegment(sketch, "E187", {"start": v(6.56, 23.47) * mm, "end": v(20.02, 23.47) * mm});
            skLineSegment(sketch, "E188", {"start": v(20.02, 23.47) * mm, "end": v(20.02, 24.04) * mm});
            skLineSegment(sketch, "E189", {"start": v(20.02, 24.04) * mm, "end": v(6.56, 24.04) * mm});
            skLineSegment(sketch, "E190", {"start": v(6.56, 23.47) * mm, "end": v(5.9, 23.68) * mm});
            skLineSegment(sketch, "E191", {"start": v(5.9, 23.68) * mm, "end": v(5.9, 23.83) * mm});
            skLineSegment(sketch, "E192", {"start": v(5.9, 23.83) * mm, "end": v(6.56, 24.04) * mm});
            skSolve(sketch);
        }
        {
            var Q0;
            Q0=makeQuery(id+"F75.imprint","IMPRINT",FACE,{"disambiguationData":[TD([[makeQuery(id+"F75.imprint","IMPRINT",EDGE,{"derivedFrom":sQuery(id+"F75.wireOp",EDGE,"E187")}),-1.0]])]});
            var Q1;
            Q1=makeQuery(id+"F75.imprint","IMPRINT",FACE,{"disambiguationData":[TD([[makeQuery(id+"F75.imprint","IMPRINT",EDGE,{"derivedFrom":sQuery(id+"F75.wireOp",EDGE,"E181")}),-1.0]])]});
            extrude(context, id + "F76", {"entities" : qUnion([Q0, Q1]), "operationType" : NewBodyOperationType.ADD, "depth" : 0.5 * mm});
        }
        {
            var Q0;
            {var subQ0=sQuery(id+"F0.wireOp",EDGE,"E9");Q0=makeQuery(id+"F2.boolean.opBoolean","MERGE",FACE,{"derivedFrom":[makeQuery(id+"F1.opExtrude","SWEPT_FACE",FACE,{"disambiguationData":[OSD([subQ0])]}),makeQuery(id+"F2.opExtrude","SWEPT_FACE",FACE,{"disambiguationData":[OSD([subQ0])]})]});}
            var sketch = newSketch(context, id + "F77", { "sketchPlane" : qUnion([Q0])});
            skCircle(sketch, "E193", {"center": v(-2.34, 23.81) * mm, "radius": 0.1 * mm});
            skSolve(sketch);
        }
        {
            var Q0;
            Q0=makeQuery(id+"F77.imprint","IMPRINT",FACE,{"disambiguationData":[TD([[makeQuery(id+"F77.imprint","IMPRINT",EDGE,{"derivedFrom":sQuery(id+"F77.wireOp",EDGE,"E193")}),1.0]])]});
            extrude(context, id + "F78", {"entities" : qUnion([Q0]), "operationType" : NewBodyOperationType.ADD, "depth" : 25.4 * mm});
        }
        {
            var Q0;
            {var subQ0=sQuery(id+"F0.wireOp",EDGE,"E16");var subQ5=sQuery(id+"F0.wireOp",EDGE,"E4");var subQ8=sQuery(id+"F0.wireOp",EDGE,"E17");var subQ11=sQuery(id+"F0.wireOp",EDGE,"E11");var subQ13=sQuery(id+"F0.wireOp",EDGE,"E0");var subQ27=sQuery(id+"F0.wireOp",EDGE,"E20");Q0=makeQuery(id+"F7.boolean.opBoolean","SPLIT",FACE,{"disambiguationData":[TD([makeQuery(id+"F5.opShell","OFFSET_FACE",FACE,{"disambiguationData":[OSD([subQ27])]})])],"derivedFrom":makeQuery(id+"F5.opShell","OFFSET_FACE",FACE,{"disambiguationData":[OSD([subQ13,subQ5,subQ11,subQ0,subQ8])]})});}
            var sketch = newSketch(context, id + "F79", { "sketchPlane" : qUnion([Q0])});
            skCircle(sketch, "E194", {"center": v(55.43, 20.45) * mm, "radius": 1.37 * mm});
            skCircle(sketch, "E195", {"center": v(55.44, -20.32) * mm, "radius": 1.29 * mm});
            skSolve(sketch);
        }
        {
            var Q0;
            Q0=makeQuery(id+"F79.imprint","IMPRINT",FACE,{"disambiguationData":[TD([[makeQuery(id+"F79.imprint","IMPRINT",EDGE,{"derivedFrom":sQuery(id+"F79.wireOp",EDGE,"E195")}),1.0]])]});
            var Q1;
            Q1=makeQuery(id+"F79.imprint","IMPRINT",FACE,{"disambiguationData":[TD([[makeQuery(id+"F79.imprint","IMPRINT",EDGE,{"derivedFrom":sQuery(id+"F79.wireOp",EDGE,"E194")}),1.0]])]});
            extrude(context, id + "F80", {"entities" : qUnion([Q0, Q1]), "operationType" : NewBodyOperationType.ADD, "depth" : 39.37 * mm});
        }
        {
            var Q0;
            Q0=makeQuery(id+"F38.opExtrude","CAP_EDGE",EDGE,{"disambiguationData":[OSD([sQuery(id+"F37.wireOp",EDGE,"E122")])],"isStart":true});
            var Q1;
            Q1=makeQuery(id+"F38.opExtrude","CAP_EDGE",EDGE,{"disambiguationData":[OSD([sQuery(id+"F37.wireOp",EDGE,"E122")])],"isStart":false});
            var Q2;
            Q2=makeQuery(id+"F38.opExtrude","CAP_EDGE",EDGE,{"disambiguationData":[OSD([sQuery(id+"F37.wireOp",EDGE,"E124")])],"isStart":true});
            var Q3;
            Q3=makeQuery(id+"F38.opExtrude","SWEPT_EDGE",EDGE,{"disambiguationData":[OSD([sQuery(id+"F37.wireOp",EDGE,"E122"),sQuery(id+"F37.wireOp",EDGE,"E125")])]});
            var Q4;
            Q4=makeQuery(id+"F38.opExtrude","CAP_EDGE",EDGE,{"disambiguationData":[OSD([sQuery(id+"F37.wireOp",EDGE,"E124")])],"isStart":false});
            var Q5;
            Q5=makeQuery(id+"F39.opExtrude","CAP_EDGE",EDGE,{"disambiguationData":[OSD([sQuery(id+"F37.wireOp",EDGE,"E122")])],"isStart":false});
            var Q6;
            Q6=makeQuery(id+"F39.opExtrude","CAP_EDGE",EDGE,{"disambiguationData":[OSD([sQuery(id+"F37.wireOp",EDGE,"E124")])],"isStart":false});
            var Q7;
            Q7=makeQuery(id+"F39.opExtrude","CAP_EDGE",EDGE,{"disambiguationData":[OSD([sQuery(id+"F37.wireOp",EDGE,"E122")])],"isStart":true});
            var Q8;
            Q8=makeQuery(id+"F39.opExtrude","SWEPT_EDGE",EDGE,{"disambiguationData":[OSD([sQuery(id+"F37.wireOp",EDGE,"E122"),sQuery(id+"F37.wireOp",EDGE,"E125")])]});
            var Q9;
            Q9=makeQuery(id+"F39.opExtrude","CAP_EDGE",EDGE,{"disambiguationData":[OSD([sQuery(id+"F37.wireOp",EDGE,"E124")])],"isStart":true});
            fillet(context, id + "F81", {"entities" : qUnion([Q0, Q1, Q2, Q3, Q4, Q5, Q6, Q7, Q8, Q9]), "radius" : 0.76 * mm, "tangentPropagation" : true, "allowEdgeOverflow" : false});
        }
        {
            var Q0;
            {var subQ0=sQuery(id+"F0.wireOp",EDGE,"E16");var subQ5=sQuery(id+"F0.wireOp",EDGE,"E4");var subQ8=sQuery(id+"F0.wireOp",EDGE,"E17");var subQ11=sQuery(id+"F0.wireOp",EDGE,"E11");var subQ13=sQuery(id+"F0.wireOp",EDGE,"E0");var subQ27=sQuery(id+"F0.wireOp",EDGE,"E20");Q0=makeQuery(id+"F7.boolean.opBoolean","SPLIT",FACE,{"disambiguationData":[TD([makeQuery(id+"F5.opShell","OFFSET_FACE",FACE,{"disambiguationData":[OSD([subQ27])]})])],"derivedFrom":makeQuery(id+"F5.opShell","OFFSET_FACE",FACE,{"disambiguationData":[OSD([subQ13,subQ5,subQ11,subQ0,subQ8])]})});}
            var sketch = newSketch(context, id + "F82", { "sketchPlane" : qUnion([Q0])});
            skLineSegment(sketch, "E196", {"start": v(56.58, 21.82) * mm, "end": v(54.06, 21.82) * mm});
            skPoint(sketch, "E196.startSnap0", {"position": v(56.58, 22.86) * mm});
            skLineSegment(sketch, "E197", {"start": v(54.06, 21.82) * mm, "end": v(54.06, -21.83) * mm});
            skLineSegment(sketch, "E198", {"start": v(54.06, -21.83) * mm, "end": v(56.58, -21.83) * mm});
            skLineSegment(sketch, "E199", {"start": v(56.58, -21.83) * mm, "end": v(56.58, 21.82) * mm});
            skSolve(sketch);
        }
        {
            var Q0;
            {var subQ4=sQuery(id+"F82.wireOp",EDGE,"E197");Q0=makeQuery(id+"F82.imprint","IMPRINT",FACE,{"disambiguationData":[TD([[makeQuery(id+"F82.imprint","IMPRINT",EDGE,{"derivedFrom":subQ4}),1.0]])]});}
            extrude(context, id + "F83", {"entities" : qUnion([Q0]), "operationType" : NewBodyOperationType.ADD, "depth" : 41.43 * mm, "hasSecondDirection" : true, "secondDirectionOppositeDirection" : false, "secondDirectionDepth" : 38.3 * mm});
        }
        {
            var Q0;
            Q0=makeQuery(id+"F83.opExtrude","CAP_FACE",FACE,{"disambiguationData":[OSD([sQuery(id+"F79.wireOp",EDGE,"E194"),sQuery(id+"F79.wireOp",EDGE,"E195"),sQuery(id+"F82.wireOp",EDGE,"E196"),sQuery(id+"F82.wireOp",EDGE,"E197"),sQuery(id+"F82.wireOp",EDGE,"E198"),sQuery(id+"F82.wireOp",EDGE,"E199")])],"isStart":false});
            var sketch = newSketch(context, id + "F84", { "sketchPlane" : qUnion([Q0])});
            skLineSegment(sketch, "E200", {"start": v(54.06, 21.82) * mm, "end": v(56.58, 21.82) * mm});
            skLineSegment(sketch, "E201", {"start": v(56.58, 21.82) * mm, "end": v(56.58, -21.83) * mm});
            skLineSegment(sketch, "E202", {"start": v(56.58, -21.83) * mm, "end": v(54.06, -21.83) * mm});
            skLineSegment(sketch, "E203", {"start": v(54.06, -21.83) * mm, "end": v(54.06, 21.82) * mm});
            skSolve(sketch);
        }
        {
            var Q0;
            {var subQ1=makeQuery(id+"F83.opExtrude","CAP_EDGE",EDGE,{"disambiguationData":[OSD([sQuery(id+"F79.wireOp",EDGE,"E194")])],"isStart":false});Q0=makeQuery(id+"F84.imprint","IMPRINT",FACE,{"disambiguationData":[TD([[makeQuery(id+"F84.imprint","IMPRINT",EDGE,{"derivedFrom":subQ1}),1.0]])]});}
            var Q1;
            {var subQ1=makeQuery(id+"F83.opExtrude","CAP_EDGE",EDGE,{"disambiguationData":[OSD([sQuery(id+"F79.wireOp",EDGE,"E195")])],"isStart":false});Q1=makeQuery(id+"F84.imprint","IMPRINT",FACE,{"disambiguationData":[TD([[makeQuery(id+"F84.imprint","IMPRINT",EDGE,{"derivedFrom":subQ1}),1.0]])]});}
            extrude(context, id + "F85", {"entities" : qUnion([Q0, Q1]), "operationType" : NewBodyOperationType.ADD, "oppositeDirection" : true, "depth" : 2.3 * mm});
        }
        {
            var Q0;
            {var subQ0=sQuery(id+"F84.wireOp",EDGE,"E201");var subQ1=sQuery(id+"F79.wireOp",EDGE,"E195");var subQ2=makeQuery(id+"F83.opExtrude","CAP_EDGE",EDGE,{"disambiguationData":[OSD([subQ1])],"isStart":false});var subQ3=sQuery(id+"F79.wireOp",EDGE,"E194");var subQ4=sQuery(id+"F82.wireOp",EDGE,"E199");var subQ5=makeQuery(id+"F80.opExtrude","CAP_EDGE",EDGE,{"disambiguationData":[OSD([subQ1])],"isStart":true});Q0=makeQuery(id+"F85.boolean.opBoolean","MERGE",EDGE,{"derivedFrom":[makeQuery(id+"F83.opExtrude","CAP_EDGE",EDGE,{"disambiguationData":[OSD([subQ4]),TDD([makeQuery(id+"F82.imprint","IMPRINT",EDGE,{"disambiguationData":[TD([[makeQuery(id+"F82.imprint","INTERSECT",VERTEX,{"derivedFrom":[sQuery(id+"F82.wireOp",EDGE,"E198"),subQ4]}),-1.0]])],"derivedFrom":subQ4})])],"isStart":false}),makeQuery(id+"F83.opExtrude","CAP_EDGE",EDGE,{"disambiguationData":[OSD([subQ4]),TDD([makeQuery(id+"F82.imprint","IMPRINT",EDGE,{"disambiguationData":[TD([[makeQuery(id+"F82.imprint","INTERSECT",VERTEX,{"disambiguationData":[OD(1.0)],"derivedFrom":[subQ5,subQ4]}),-1.0]])],"derivedFrom":subQ4})])],"isStart":false}),makeQuery(id+"F85.opExtrude","CAP_EDGE",EDGE,{"disambiguationData":[OSD([subQ0]),TDD([makeQuery(id+"F84.imprint","IMPRINT",EDGE,{"disambiguationData":[TD([[makeQuery(id+"F84.imprint","INTERSECT",VERTEX,{"derivedFrom":[makeQuery(id+"F83.opExtrude","CAP_EDGE",EDGE,{"disambiguationData":[OSD([subQ3])],"isStart":false}),subQ0]}),1.0],[makeQuery(id+"F84.imprint","INTERSECT",VERTEX,{"derivedFrom":[sQuery(id+"F84.wireOp",EDGE,"E200"),subQ0]}),-1.0]])],"derivedFrom":subQ0})])],"isStart":true}),makeQuery(id+"F85.opExtrude","CAP_EDGE",EDGE,{"disambiguationData":[OSD([subQ0]),TDD([makeQuery(id+"F84.imprint","IMPRINT",EDGE,{"disambiguationData":[TD([[makeQuery(id+"F84.imprint","INTERSECT",VERTEX,{"disambiguationData":[OD(0.0)],"derivedFrom":[subQ2,subQ0]}),1.0],[makeQuery(id+"F84.imprint","INTERSECT",VERTEX,{"disambiguationData":[OD(1.0)],"derivedFrom":[subQ2,subQ0]}),-1.0]])],"derivedFrom":subQ0})])],"isStart":true})]});}
            var Q1;
            Q1=makeQuery(id+"F83.opExtrude","CAP_EDGE",EDGE,{"disambiguationData":[OSD([sQuery(id+"F82.wireOp",EDGE,"E197")])],"isStart":false});
            fillet(context, id + "F86", {"entities" : qUnion([Q0, Q1]), "radius" : 1.27 * mm, "tangentPropagation" : true, "allowEdgeOverflow" : false});
        }
        {
            var Q0;
            Q0=makeQuery(id+"F4.opExtrude","CAP_FACE",FACE,{"disambiguationData":[OSD([sQuery(id+"F0.wireOp",EDGE,"E1"),sQuery(id+"F0.wireOp",EDGE,"E2"),sQuery(id+"F0.wireOp",EDGE,"E3"),sQuery(id+"F0.wireOp",EDGE,"E16")])],"isStart":false});
            var sketch = newSketch(context, id + "F87", { "sketchPlane" : qUnion([Q0])});
            skLineSegment(sketch, "E204", {"start": v(-71.6, -6.22) * mm, "end": v(-79.03, -6.22) * mm});
            skLineSegment(sketch, "E205", {"start": v(-80.71, 0) * mm, "end": v(-70.24, 0) * mm});
            skLineSegment(sketch, "E206", {"start": v(-80.71, 0) * mm, "end": v(-79.03, -6.22) * mm});
            skLineSegment(sketch, "E207", {"start": v(-70.24, 0) * mm, "end": v(-71.6, -6.22) * mm});
            skCircle(sketch, "E208", {"center": v(-75.72, -3.22) * mm, "radius": 2.07 * mm});
            skSolve(sketch);
        }
        {
            var Q0;
            Q0=makeQuery(id+"F87.imprint","IMPRINT",FACE,{"disambiguationData":[TD([[makeQuery(id+"F87.imprint","IMPRINT",EDGE,{"derivedFrom":sQuery(id+"F87.wireOp",EDGE,"E204")}),-1.0]])]});
            extrude(context, id + "F88", {"entities" : qUnion([Q0]), "operationType" : NewBodyOperationType.ADD, "oppositeDirection" : true, "depth" : 30.43 * mm});
        }
        {
            var Q0;
            Q0=makeQuery(id+"F4.opExtrude","CAP_FACE",FACE,{"disambiguationData":[OSD([sQuery(id+"F0.wireOp",EDGE,"E12"),sQuery(id+"F0.wireOp",EDGE,"E13"),sQuery(id+"F0.wireOp",EDGE,"E14"),sQuery(id+"F0.wireOp",EDGE,"E17")])],"isStart":false});
            var sketch = newSketch(context, id + "F89", { "sketchPlane" : qUnion([Q0])});
            skLineSegment(sketch, "E209", {"start": v(8.95, 0) * mm, "end": v(20.17, 0) * mm});
            skLineSegment(sketch, "E210", {"start": v(20.17, 0) * mm, "end": v(18.86, -6.18) * mm});
            skLineSegment(sketch, "E211", {"start": v(18.86, -6.18) * mm, "end": v(10.67, -6.18) * mm});
            skLineSegment(sketch, "E212", {"start": v(10.67, -6.18) * mm, "end": v(8.95, 0) * mm});
            skCircle(sketch, "E213", {"center": v(14.53, -3.52) * mm, "radius": 1.97 * mm});
            skSolve(sketch);
        }
        {
            var Q0;
            Q0=makeQuery(id+"F89.imprint","IMPRINT",FACE,{"disambiguationData":[TD([[makeQuery(id+"F89.imprint","IMPRINT",EDGE,{"derivedFrom":sQuery(id+"F89.wireOp",EDGE,"E209")}),1.0]])]});
            extrude(context, id + "F90", {"entities" : qUnion([Q0]), "operationType" : NewBodyOperationType.ADD, "oppositeDirection" : true, "depth" : 30.53 * mm});
        }
        {
            var Q0;
            Q0=makeQuery(id+"F88.opExtrude","CAP_FACE",FACE,{"disambiguationData":[OSD([sQuery(id+"F87.wireOp",EDGE,"E204"),sQuery(id+"F87.wireOp",EDGE,"E205"),sQuery(id+"F87.wireOp",EDGE,"E206"),sQuery(id+"F87.wireOp",EDGE,"E207"),sQuery(id+"F87.wireOp",EDGE,"E208")])],"isStart":false});
            var sketch = newSketch(context, id + "F91", { "sketchPlane" : qUnion([Q0])});
            skCircle(sketch, "E214", {"center": v(75.72, -3.22) * mm, "radius": 0.7 * mm});
            skCircle(sketch, "E215", {"center": v(-14.5, -3.49) * mm, "radius": 0.72 * mm});
            skSolve(sketch);
        }
        {
            var Q0;
            Q0=makeQuery(id+"F91.imprint","IMPRINT",FACE,{"disambiguationData":[TD([[makeQuery(id+"F91.imprint","IMPRINT",EDGE,{"derivedFrom":sQuery(id+"F91.wireOp",EDGE,"E214")}),1.0]])]});
            var Q1;
            Q1=makeQuery(id+"F91.imprint","IMPRINT",FACE,{"disambiguationData":[TD([[makeQuery(id+"F91.imprint","IMPRINT",EDGE,{"derivedFrom":sQuery(id+"F91.wireOp",EDGE,"E215")}),1.0]])]});
            extrude(context, id + "F92", {"entities" : qUnion([Q0, Q1]), "operationType" : NewBodyOperationType.ADD, "depth" : 10.21 * mm, "hasSecondDirection" : true, "secondDirectionOppositeDirection" : true, "secondDirectionDepth" : 40.6 * mm});
        }
        {
            var Q0;
            Q0=makeQuery(id+"F90.opExtrude","CAP_FACE",FACE,{"disambiguationData":[OSD([sQuery(id+"F89.wireOp",EDGE,"E209"),sQuery(id+"F89.wireOp",EDGE,"E210"),sQuery(id+"F89.wireOp",EDGE,"E211"),sQuery(id+"F89.wireOp",EDGE,"E212"),sQuery(id+"F89.wireOp",EDGE,"E213")])],"isStart":false});
            var sketch = newSketch(context, id + "F93", { "sketchPlane" : qUnion([Q0])});
            skCircle(sketch, "E216", {"center": v(-14.53, -3.52) * mm, "radius": 1.82 * mm});
            skCircle(sketch, "E217", {"center": v(-14.53, -3.52) * mm, "radius": 1.98 * mm});
            skSolve(sketch);
        }
        {
            var Q0;
            Q0=makeQuery(id+"F93.imprint","IMPRINT",FACE,{"disambiguationData":[TD([[makeQuery(id+"F93.imprint","IMPRINT",EDGE,{"derivedFrom":sQuery(id+"F93.wireOp",EDGE,"E216")}),1.0]])]});
            extrude(context, id + "F94", {"entities" : qUnion([Q0]), "operationType" : NewBodyOperationType.ADD, "depth" : 3.3 * mm, "hasSecondDirection" : true, "secondDirectionOppositeDirection" : false, "secondDirectionDepth" : 1.7 * mm});
        }
        {
            var Q0;
            Q0=makeQuery(id+"F93.imprint","IMPRINT",FACE,{"disambiguationData":[TD([[makeQuery(id+"F93.imprint","IMPRINT",EDGE,{"derivedFrom":sQuery(id+"F93.wireOp",EDGE,"E217")}),1.0]])]});
            var Q1;
            Q1=makeQuery(id+"F93.imprint","IMPRINT",FACE,{"disambiguationData":[TD([[makeQuery(id+"F93.imprint","IMPRINT",EDGE,{"derivedFrom":sQuery(id+"F93.wireOp",EDGE,"E216")}),-1.0]])]});
            extrude(context, id + "F95", {"entities" : qUnion([Q0, Q1]), "operationType" : NewBodyOperationType.ADD, "depth" : 10.36 * mm, "hasSecondDirection" : true, "secondDirectionOppositeDirection" : false, "secondDirectionDepth" : 1.72 * mm});
        }
        {
            var Q0;
            Q0=makeQuery(id+"F90.opExtrude","CAP_FACE",FACE,{"disambiguationData":[OSD([sQuery(id+"F89.wireOp",EDGE,"E209"),sQuery(id+"F89.wireOp",EDGE,"E210"),sQuery(id+"F89.wireOp",EDGE,"E211"),sQuery(id+"F89.wireOp",EDGE,"E212"),sQuery(id+"F89.wireOp",EDGE,"E213")])],"isStart":false});
            var sketch = newSketch(context, id + "F96", { "sketchPlane" : qUnion([Q0])});
            skCircle(sketch, "E218", {"center": v(-14.53, -3.52) * mm, "radius": 1.98 * mm});
            skCircle(sketch, "E219", {"center": v(-14.53, -3.52) * mm, "radius": 8.58 * mm});
            skSolve(sketch);
        }
        {
            var Q0;
            Q0=makeQuery(id+"F96.imprint","IMPRINT",FACE,{"disambiguationData":[TD([[makeQuery(id+"F96.imprint","IMPRINT",EDGE,{"derivedFrom":sQuery(id+"F96.wireOp",EDGE,"E219")}),1.0]])]});
            var Q1;
            Q1=makeQuery(id+"F96.imprint","IMPRINT",FACE,{"disambiguationData":[TD([[makeQuery(id+"F96.imprint","IMPRINT",EDGE,{"derivedFrom":sQuery(id+"F96.wireOp",EDGE,"E218")}),-1.0]])]});
            extrude(context, id + "F97", {"entities" : qUnion([Q0, Q1]), "operationType" : NewBodyOperationType.ADD, "depth" : 10.34 * mm, "hasSecondDirection" : true, "secondDirectionOppositeDirection" : false, "secondDirectionDepth" : 1.73 * mm});
        }
        {
            var Q0;
            Q0=makeQuery(id+"F90.boolean.opBoolean","MERGE",FACE,{"derivedFrom":[makeQuery(id+"F4.opExtrude","CAP_FACE",FACE,{"disambiguationData":[OSD([sQuery(id+"F0.wireOp",EDGE,"E12"),sQuery(id+"F0.wireOp",EDGE,"E13"),sQuery(id+"F0.wireOp",EDGE,"E14"),sQuery(id+"F0.wireOp",EDGE,"E17")])],"isStart":false}),makeQuery(id+"F90.opExtrude","CAP_FACE",FACE,{"disambiguationData":[OSD([sQuery(id+"F89.wireOp",EDGE,"E209"),sQuery(id+"F89.wireOp",EDGE,"E210"),sQuery(id+"F89.wireOp",EDGE,"E211"),sQuery(id+"F89.wireOp",EDGE,"E212"),sQuery(id+"F89.wireOp",EDGE,"E213")])],"isStart":true})]});
            var sketch = newSketch(context, id + "F98", { "sketchPlane" : qUnion([Q0])});
            skCircle(sketch, "E220", {"center": v(14.53, -3.52) * mm, "radius": 1.82 * mm});
            skCircle(sketch, "E221", {"center": v(14.53, -3.52) * mm, "radius": 1.97 * mm});
            skSolve(sketch);
        }
        {
            var Q0;
            Q0=makeQuery(id+"F98.imprint","IMPRINT",FACE,{"disambiguationData":[TD([[makeQuery(id+"F98.imprint","IMPRINT",EDGE,{"derivedFrom":sQuery(id+"F98.wireOp",EDGE,"E220")}),1.0]])]});
            extrude(context, id + "F99", {"entities" : qUnion([Q0]), "operationType" : NewBodyOperationType.ADD, "depth" : 3.76 * mm, "hasSecondDirection" : true, "secondDirectionOppositeDirection" : false, "secondDirectionDepth" : 1.8 * mm});
        }
        {
            var Q0;
            Q0=makeQuery(id+"F98.imprint","IMPRINT",FACE,{"disambiguationData":[TD([[makeQuery(id+"F98.imprint","IMPRINT",EDGE,{"derivedFrom":sQuery(id+"F98.wireOp",EDGE,"E220")}),-1.0]])]});
            extrude(context, id + "F100", {"entities" : qUnion([Q0]), "operationType" : NewBodyOperationType.ADD, "depth" : 10.4 * mm, "hasSecondDirection" : true, "secondDirectionOppositeDirection" : false, "secondDirectionDepth" : 1.83 * mm});
        }
        {
            var Q0;
            Q0=makeQuery(id+"F97.opExtrude","CAP_FACE",FACE,{"disambiguationData":[OSD([sQuery(id+"F96.wireOp",EDGE,"E218"),sQuery(id+"F96.wireOp",EDGE,"E219")])],"isStart":true});
            extrude(context, id + "F101", {"entities" : qUnion([Q0]), "depth" : 42.8 * mm, "hasSecondDirection" : true, "secondDirectionOppositeDirection" : false, "secondDirectionDepth" : 34.04 * mm});
        }
        {
            var Q0;
            Q0=makeQuery(id+"F88.boolean.opBoolean","MERGE",FACE,{"derivedFrom":[makeQuery(id+"F4.opExtrude","CAP_FACE",FACE,{"disambiguationData":[OSD([sQuery(id+"F0.wireOp",EDGE,"E1"),sQuery(id+"F0.wireOp",EDGE,"E2"),sQuery(id+"F0.wireOp",EDGE,"E3"),sQuery(id+"F0.wireOp",EDGE,"E16")])],"isStart":false}),makeQuery(id+"F88.opExtrude","CAP_FACE",FACE,{"disambiguationData":[OSD([sQuery(id+"F87.wireOp",EDGE,"E204"),sQuery(id+"F87.wireOp",EDGE,"E205"),sQuery(id+"F87.wireOp",EDGE,"E206"),sQuery(id+"F87.wireOp",EDGE,"E207"),sQuery(id+"F87.wireOp",EDGE,"E208")])],"isStart":true})]});
            var sketch = newSketch(context, id + "F102", { "sketchPlane" : qUnion([Q0])});
            skCircle(sketch, "E222", {"center": v(-75.72, -3.22) * mm, "radius": 1.9 * mm});
            skCircle(sketch, "E223", {"center": v(-75.72, -3.22) * mm, "radius": 2.1 * mm});
            skSolve(sketch);
        }
        {
            var Q0;
            Q0=makeQuery(id+"F102.imprint","IMPRINT",FACE,{"disambiguationData":[TD([[makeQuery(id+"F102.imprint","IMPRINT",EDGE,{"derivedFrom":sQuery(id+"F102.wireOp",EDGE,"E222")}),1.0]])]});
            extrude(context, id + "F103", {"entities" : qUnion([Q0]), "operationType" : NewBodyOperationType.ADD, "depth" : 3.63 * mm, "hasSecondDirection" : true, "secondDirectionOppositeDirection" : false, "secondDirectionDepth" : 1.78 * mm});
        }
        {
            var Q0;
            Q0=makeQuery(id+"F102.imprint","IMPRINT",FACE,{"disambiguationData":[TD([[makeQuery(id+"F102.imprint","IMPRINT",EDGE,{"derivedFrom":sQuery(id+"F102.wireOp",EDGE,"E222")}),-1.0]])]});
            var Q1;
            Q1=makeQuery(id+"F102.imprint","IMPRINT",FACE,{"disambiguationData":[TD([[makeQuery(id+"F102.imprint","IMPRINT",EDGE,{"derivedFrom":sQuery(id+"F102.wireOp",EDGE,"E223")}),1.0]])]});
            extrude(context, id + "F104", {"entities" : qUnion([Q0, Q1]), "operationType" : NewBodyOperationType.ADD, "depth" : 10.36 * mm, "hasSecondDirection" : true, "secondDirectionOppositeDirection" : false, "secondDirectionDepth" : 1.78 * mm});
        }
        {
            var Q0;
            Q0=makeQuery(id+"F88.opExtrude","CAP_FACE",FACE,{"disambiguationData":[OSD([sQuery(id+"F87.wireOp",EDGE,"E204"),sQuery(id+"F87.wireOp",EDGE,"E205"),sQuery(id+"F87.wireOp",EDGE,"E206"),sQuery(id+"F87.wireOp",EDGE,"E207"),sQuery(id+"F87.wireOp",EDGE,"E208")])],"isStart":false});
            var sketch = newSketch(context, id + "F105", { "sketchPlane" : qUnion([Q0])});
            skCircle(sketch, "E224", {"center": v(75.72, -3.22) * mm, "radius": 2 * mm});
            skCircle(sketch, "E225", {"center": v(75.72, -3.22) * mm, "radius": 2.08 * mm});
            skSolve(sketch);
        }
        {
            var Q0;
            Q0=makeQuery(id+"F105.imprint","IMPRINT",FACE,{"disambiguationData":[TD([[makeQuery(id+"F105.imprint","IMPRINT",EDGE,{"derivedFrom":sQuery(id+"F105.wireOp",EDGE,"E224")}),1.0]])]});
            extrude(context, id + "F106", {"entities" : qUnion([Q0]), "operationType" : NewBodyOperationType.ADD, "depth" : 3.63 * mm, "hasSecondDirection" : true, "secondDirectionOppositeDirection" : false, "secondDirectionDepth" : 1.83 * mm});
        }
        {
            var Q0;
            Q0=makeQuery(id+"F105.imprint","IMPRINT",FACE,{"disambiguationData":[TD([[makeQuery(id+"F105.imprint","IMPRINT",EDGE,{"derivedFrom":sQuery(id+"F105.wireOp",EDGE,"E224")}),-1.0]])]});
            var Q1;
            Q1=makeQuery(id+"F105.imprint","IMPRINT",FACE,{"disambiguationData":[TD([[makeQuery(id+"F105.imprint","IMPRINT",EDGE,{"derivedFrom":sQuery(id+"F105.wireOp",EDGE,"E225")}),1.0]])]});
            extrude(context, id + "F107", {"entities" : qUnion([Q0, Q1]), "depth" : 10.16 * mm});
        }
        {
            var Q0;
            Q0=makeQuery(id+"F88.boolean.opBoolean","MERGE",FACE,{"derivedFrom":[makeQuery(id+"F4.opExtrude","CAP_FACE",FACE,{"disambiguationData":[OSD([sQuery(id+"F0.wireOp",EDGE,"E1"),sQuery(id+"F0.wireOp",EDGE,"E2"),sQuery(id+"F0.wireOp",EDGE,"E3"),sQuery(id+"F0.wireOp",EDGE,"E16")])],"isStart":false}),makeQuery(id+"F88.opExtrude","CAP_FACE",FACE,{"disambiguationData":[OSD([sQuery(id+"F87.wireOp",EDGE,"E204"),sQuery(id+"F87.wireOp",EDGE,"E205"),sQuery(id+"F87.wireOp",EDGE,"E206"),sQuery(id+"F87.wireOp",EDGE,"E207"),sQuery(id+"F87.wireOp",EDGE,"E208")])],"isStart":true})]});
            var sketch = newSketch(context, id + "F108", { "sketchPlane" : qUnion([Q0])});
            skCircle(sketch, "E226", {"center": v(-75.72, -3.22) * mm, "radius": 8.93 * mm});
            skSolve(sketch);
        }
        {
            var Q0;
            {var subQ2=sQuery(id+"F87.wireOp",EDGE,"E204");Q0=makeQuery(id+"F108.imprint","IMPRINT",FACE,{"disambiguationData":[TD([[makeQuery(id+"F108.imprint","IMPRINT",EDGE,{"derivedFrom":makeQuery(id+"F88.opExtrude","CAP_EDGE",EDGE,{"disambiguationData":[OSD([subQ2])],"isStart":true})}),1.0]])]});}
            var Q1;
            {var subQ4=sQuery(id+"F87.wireOp",EDGE,"E204");Q1=makeQuery(id+"F108.imprint","IMPRINT",FACE,{"disambiguationData":[TD([[makeQuery(id+"F108.imprint","IMPRINT",EDGE,{"derivedFrom":makeQuery(id+"F88.opExtrude","CAP_EDGE",EDGE,{"disambiguationData":[OSD([subQ4])],"isStart":true})}),-1.0]])]});}
            extrude(context, id + "F109", {"entities" : qUnion([Q0, Q1]), "operationType" : NewBodyOperationType.ADD, "depth" : 10.5 * mm, "hasSecondDirection" : true, "secondDirectionOppositeDirection" : false, "secondDirectionDepth" : 1.75 * mm});
        }
        {
            var Q0;
            {var subQ2=sQuery(id+"F87.wireOp",EDGE,"E204");Q0=makeQuery(id+"F108.imprint","IMPRINT",FACE,{"disambiguationData":[TD([[makeQuery(id+"F108.imprint","IMPRINT",EDGE,{"derivedFrom":makeQuery(id+"F88.opExtrude","CAP_EDGE",EDGE,{"disambiguationData":[OSD([subQ2])],"isStart":true})}),1.0]])]});}
            var Q1;
            {var subQ4=sQuery(id+"F87.wireOp",EDGE,"E204");Q1=makeQuery(id+"F108.imprint","IMPRINT",FACE,{"disambiguationData":[TD([[makeQuery(id+"F108.imprint","IMPRINT",EDGE,{"derivedFrom":makeQuery(id+"F88.opExtrude","CAP_EDGE",EDGE,{"disambiguationData":[OSD([subQ4])],"isStart":true})}),-1.0]])]});}
            extrude(context, id + "F110", {"entities" : qUnion([Q0, Q1]), "operationType" : NewBodyOperationType.ADD, "oppositeDirection" : true, "depth" : 40.74 * mm, "hasSecondDirection" : true, "secondDirectionOppositeDirection" : true, "secondDirectionDepth" : 32.1 * mm});
        }
        {
            var Q0;
            {var subQ0=sQuery(id+"F0.wireOp",EDGE,"E12");var subQ1=sQuery(id+"F0.wireOp",EDGE,"E13");var subQ2=sQuery(id+"F0.wireOp",EDGE,"E14");Q0=makeQuery(id+"F3.boolean.opBoolean","SPLIT",EDGE,{"disambiguationData":[TD([makeQuery(id+"F3.opExtrude","CAP_FACE",FACE,{"disambiguationData":[OSD([subQ0,subQ1,subQ2,sQuery(id+"F0.wireOp",EDGE,"E17")])],"isStart":false})])],"derivedFrom":makeQuery(id+"F2.boolean.opBoolean","MERGE",EDGE,{"derivedFrom":[makeQuery(id+"F1.opExtrude","SWEPT_EDGE",EDGE,{"disambiguationData":[OSD([subQ0,subQ1])]}),makeQuery(id+"F2.opExtrude","SWEPT_EDGE",EDGE,{"disambiguationData":[OSD([subQ0,subQ1])]})]})});}
            var Q1;
            {var subQ0=sQuery(id+"F0.wireOp",EDGE,"E13");var subQ1=sQuery(id+"F0.wireOp",EDGE,"E14");var subQ2=sQuery(id+"F0.wireOp",EDGE,"E12");Q1=makeQuery(id+"F3.boolean.opBoolean","SPLIT",EDGE,{"disambiguationData":[TD([makeQuery(id+"F3.opExtrude","CAP_FACE",FACE,{"disambiguationData":[OSD([subQ2,subQ0,subQ1,sQuery(id+"F0.wireOp",EDGE,"E17")])],"isStart":false})])],"derivedFrom":makeQuery(id+"F2.boolean.opBoolean","MERGE",EDGE,{"derivedFrom":[makeQuery(id+"F1.opExtrude","SWEPT_EDGE",EDGE,{"disambiguationData":[OSD([subQ0,subQ1])]}),makeQuery(id+"F2.opExtrude","SWEPT_EDGE",EDGE,{"disambiguationData":[OSD([subQ0,subQ1])]})]})});}
            var Q2;
            {var subQ0=sQuery(id+"F0.wireOp",EDGE,"E1");var subQ1=sQuery(id+"F0.wireOp",EDGE,"E2");var subQ2=sQuery(id+"F0.wireOp",EDGE,"E3");Q2=makeQuery(id+"F3.boolean.opBoolean","SPLIT",EDGE,{"disambiguationData":[TD([makeQuery(id+"F3.opExtrude","CAP_FACE",FACE,{"disambiguationData":[OSD([subQ0,subQ1,subQ2,sQuery(id+"F0.wireOp",EDGE,"E16")])],"isStart":false})])],"derivedFrom":makeQuery(id+"F2.boolean.opBoolean","MERGE",EDGE,{"derivedFrom":[makeQuery(id+"F1.opExtrude","SWEPT_EDGE",EDGE,{"disambiguationData":[OSD([subQ0,subQ1])]}),makeQuery(id+"F2.opExtrude","SWEPT_EDGE",EDGE,{"disambiguationData":[OSD([subQ0,subQ1])]})]})});}
            var Q3;
            {var subQ0=sQuery(id+"F0.wireOp",EDGE,"E2");var subQ1=sQuery(id+"F0.wireOp",EDGE,"E3");var subQ2=sQuery(id+"F0.wireOp",EDGE,"E1");Q3=makeQuery(id+"F3.boolean.opBoolean","SPLIT",EDGE,{"disambiguationData":[TD([makeQuery(id+"F3.opExtrude","CAP_FACE",FACE,{"disambiguationData":[OSD([subQ2,subQ0,subQ1,sQuery(id+"F0.wireOp",EDGE,"E16")])],"isStart":false})])],"derivedFrom":makeQuery(id+"F2.boolean.opBoolean","MERGE",EDGE,{"derivedFrom":[makeQuery(id+"F1.opExtrude","SWEPT_EDGE",EDGE,{"disambiguationData":[OSD([subQ0,subQ1])]}),makeQuery(id+"F2.opExtrude","SWEPT_EDGE",EDGE,{"disambiguationData":[OSD([subQ0,subQ1])]})]})});}
            var Q4;
            {var subQ0=sQuery(id+"F0.wireOp",EDGE,"E1");var subQ1=sQuery(id+"F0.wireOp",EDGE,"E2");var subQ2=sQuery(id+"F0.wireOp",EDGE,"E3");Q4=makeQuery(id+"F3.boolean.opBoolean","SPLIT",EDGE,{"disambiguationData":[TD([makeQuery(id+"F3.opExtrude","CAP_FACE",FACE,{"disambiguationData":[OSD([subQ0,subQ1,subQ2,sQuery(id+"F0.wireOp",EDGE,"E16")])],"isStart":true})])],"derivedFrom":makeQuery(id+"F2.boolean.opBoolean","MERGE",EDGE,{"derivedFrom":[makeQuery(id+"F1.opExtrude","SWEPT_EDGE",EDGE,{"disambiguationData":[OSD([subQ0,subQ1])]}),makeQuery(id+"F2.opExtrude","SWEPT_EDGE",EDGE,{"disambiguationData":[OSD([subQ0,subQ1])]})]})});}
            var Q5;
            {var subQ0=sQuery(id+"F0.wireOp",EDGE,"E3");var subQ1=sQuery(id+"F0.wireOp",EDGE,"E2");var subQ2=sQuery(id+"F0.wireOp",EDGE,"E1");Q5=makeQuery(id+"F3.boolean.opBoolean","SPLIT",EDGE,{"disambiguationData":[TD([makeQuery(id+"F3.opExtrude","CAP_FACE",FACE,{"disambiguationData":[OSD([subQ2,subQ1,subQ0,sQuery(id+"F0.wireOp",EDGE,"E16")])],"isStart":true})])],"derivedFrom":makeQuery(id+"F2.boolean.opBoolean","MERGE",EDGE,{"derivedFrom":[makeQuery(id+"F1.opExtrude","SWEPT_EDGE",EDGE,{"disambiguationData":[OSD([subQ1,subQ0])]}),makeQuery(id+"F2.opExtrude","SWEPT_EDGE",EDGE,{"disambiguationData":[OSD([subQ1,subQ0])]})]})});}
            var Q6;
            {var subQ0=sQuery(id+"F0.wireOp",EDGE,"E14");var subQ1=sQuery(id+"F0.wireOp",EDGE,"E13");var subQ2=sQuery(id+"F0.wireOp",EDGE,"E12");Q6=makeQuery(id+"F3.boolean.opBoolean","SPLIT",EDGE,{"disambiguationData":[TD([makeQuery(id+"F3.opExtrude","CAP_FACE",FACE,{"disambiguationData":[OSD([subQ2,subQ1,subQ0,sQuery(id+"F0.wireOp",EDGE,"E17")])],"isStart":true})])],"derivedFrom":makeQuery(id+"F2.boolean.opBoolean","MERGE",EDGE,{"derivedFrom":[makeQuery(id+"F1.opExtrude","SWEPT_EDGE",EDGE,{"disambiguationData":[OSD([subQ1,subQ0])]}),makeQuery(id+"F2.opExtrude","SWEPT_EDGE",EDGE,{"disambiguationData":[OSD([subQ1,subQ0])]})]})});}
            var Q7;
            {var subQ0=sQuery(id+"F0.wireOp",EDGE,"E14");var subQ1=sQuery(id+"F0.wireOp",EDGE,"E13");var subQ2=sQuery(id+"F0.wireOp",EDGE,"E12");Q7=makeQuery(id+"F3.boolean.opBoolean","SPLIT",EDGE,{"disambiguationData":[TD([makeQuery(id+"F3.opExtrude","CAP_FACE",FACE,{"disambiguationData":[OSD([subQ2,subQ1,subQ0,sQuery(id+"F0.wireOp",EDGE,"E17")])],"isStart":true})])],"derivedFrom":makeQuery(id+"F2.boolean.opBoolean","MERGE",EDGE,{"derivedFrom":[makeQuery(id+"F1.opExtrude","SWEPT_EDGE",EDGE,{"disambiguationData":[OSD([subQ2,subQ1])]}),makeQuery(id+"F2.opExtrude","SWEPT_EDGE",EDGE,{"disambiguationData":[OSD([subQ2,subQ1])]})]})});}
            fillet(context, id + "F111", {"entities" : qUnion([Q0, Q1, Q2, Q3, Q4, Q5, Q6, Q7]), "radius" : 5.08 * mm, "tangentPropagation" : true, "allowEdgeOverflow" : false});
        }
        {
            var Q0;
            Q0=makeQuery(id+"F1.opExtrude","CAP_EDGE",EDGE,{"disambiguationData":[OSD([sQuery(id+"F0.wireOp",EDGE,"E0")])],"isStart":false});
            var Q1;
            Q1=makeQuery(id+"F1.opExtrude","CAP_EDGE",EDGE,{"disambiguationData":[OSD([sQuery(id+"F0.wireOp",EDGE,"E4")])],"isStart":false});
            var Q2;
            Q2=makeQuery(id+"F1.opExtrude","CAP_EDGE",EDGE,{"disambiguationData":[OSD([sQuery(id+"F0.wireOp",EDGE,"E11")])],"isStart":false});
            var Q3;
            Q3=makeQuery(id+"F2.opExtrude","CAP_EDGE",EDGE,{"disambiguationData":[OSD([sQuery(id+"F0.wireOp",EDGE,"E0")])],"isStart":false});
            var Q4;
            Q4=makeQuery(id+"F2.opExtrude","CAP_EDGE",EDGE,{"disambiguationData":[OSD([sQuery(id+"F0.wireOp",EDGE,"E11")])],"isStart":false});
            var Q5;
            Q5=makeQuery(id+"F2.opExtrude","CAP_EDGE",EDGE,{"disambiguationData":[OSD([sQuery(id+"F0.wireOp",EDGE,"E4")])],"isStart":false});
            var Q6;
            Q6=makeQuery(id+"F7.boolean.opBoolean","MERGE",EDGE,{"derivedFrom":[makeQuery(id+"F1.opExtrude","CAP_EDGE",EDGE,{"disambiguationData":[OSD([sQuery(id+"F0.wireOp",EDGE,"E7")])],"isStart":false}),makeQuery(id+"F7.opExtrude","CAP_EDGE",EDGE,{"disambiguationData":[OSD([sQuery(id+"F6.wireOp",EDGE,"E38")])],"isStart":true})]});
            var Q7;
            Q7=makeQuery(id+"F7.boolean.opBoolean","MERGE",EDGE,{"derivedFrom":[makeQuery(id+"F2.opExtrude","CAP_EDGE",EDGE,{"disambiguationData":[OSD([sQuery(id+"F0.wireOp",EDGE,"E7")])],"isStart":false}),makeQuery(id+"F7.opExtrude","CAP_EDGE",EDGE,{"disambiguationData":[OSD([sQuery(id+"F6.wireOp",EDGE,"E40")])],"isStart":true})]});
            fillet(context, id + "F112", {"entities" : qUnion([Q0, Q1, Q2, Q3, Q4, Q5, Q6, Q7]), "radius" : 2.3 * mm, "tangentPropagation" : true, "allowEdgeOverflow" : false});
        }
        {
            var Q0;
            {var subQ0=sQuery(id+"F0.wireOp",EDGE,"E16");var subQ5=sQuery(id+"F0.wireOp",EDGE,"E4");var subQ8=sQuery(id+"F0.wireOp",EDGE,"E17");var subQ11=sQuery(id+"F0.wireOp",EDGE,"E11");var subQ13=sQuery(id+"F0.wireOp",EDGE,"E0");var subQ27=sQuery(id+"F0.wireOp",EDGE,"E20");Q0=makeQuery(id+"F7.boolean.opBoolean","SPLIT",FACE,{"disambiguationData":[TD([makeQuery(id+"F5.opShell","OFFSET_FACE",FACE,{"disambiguationData":[OSD([subQ27])]})])],"derivedFrom":makeQuery(id+"F5.opShell","OFFSET_FACE",FACE,{"disambiguationData":[OSD([subQ13,subQ5,subQ11,subQ0,subQ8])]})});}
            var sketch = newSketch(context, id + "F113", { "sketchPlane" : qUnion([Q0])});
            skCircle(sketch, "E227", {"center": v(55.25, 8.89) * mm, "radius": 1.25 * mm});
            skCircle(sketch, "E228", {"center": v(55.47, -3.58) * mm, "radius": 1.24 * mm});
            skSolve(sketch);
        }
        {
            var Q0;
            Q0=makeQuery(id+"F113.imprint","IMPRINT",FACE,{"disambiguationData":[TD([[makeQuery(id+"F113.imprint","IMPRINT",EDGE,{"derivedFrom":sQuery(id+"F113.wireOp",EDGE,"E227")}),1.0]])]});
            var Q1;
            Q1=makeQuery(id+"F113.imprint","IMPRINT",FACE,{"disambiguationData":[TD([[makeQuery(id+"F113.imprint","IMPRINT",EDGE,{"derivedFrom":sQuery(id+"F113.wireOp",EDGE,"E228")}),1.0]])]});
            extrude(context, id + "F114", {"entities" : qUnion([Q0, Q1]), "operationType" : NewBodyOperationType.ADD, "depth" : 44.45 * mm, "hasSecondDirection" : true, "secondDirectionOppositeDirection" : false, "secondDirectionDepth" : 38.35 * mm});
        }
        {
            var Q0;
            Q0=makeQuery(id+"F114.opExtrude","CAP_EDGE",EDGE,{"disambiguationData":[OSD([sQuery(id+"F113.wireOp",EDGE,"E228")])],"isStart":false});
            var Q1;
            Q1=makeQuery(id+"F114.opExtrude","CAP_EDGE",EDGE,{"disambiguationData":[OSD([sQuery(id+"F113.wireOp",EDGE,"E227")])],"isStart":false});
            fillet(context, id + "F115", {"entities" : qUnion([Q0, Q1]), "radius" : 1.17 * mm, "tangentPropagation" : true, "allowEdgeOverflow" : false});
        }
        {
            var Q0;
            Q0=makeQuery(id+"F106.opExtrude","CAP_FACE",FACE,{"disambiguationData":[OSD([sQuery(id+"F105.wireOp",EDGE,"E224")])],"isStart":false});
            var sketch = newSketch(context, id + "F116", { "sketchPlane" : qUnion([Q0])});
            skCircle(sketch, "E229", {"center": v(77.1, -3.21) * mm, "radius": 0.44 * mm});
            skCircle(sketch, "E230", {"center": v(75.73, -4.58) * mm, "radius": 0.45 * mm});
            skCircle(sketch, "E231", {"center": v(74.35, -3.21) * mm, "radius": 0.44 * mm});
            skCircle(sketch, "E232", {"center": v(75.73, -1.9) * mm, "radius": 0.44 * mm});
            skSolve(sketch);
        }
        {
            var Q0;
            Q0=makeQuery(id+"F116.imprint","IMPRINT",FACE,{"disambiguationData":[TD([[makeQuery(id+"F116.imprint","IMPRINT",EDGE,{"derivedFrom":sQuery(id+"F116.wireOp",EDGE,"E229")}),1.0]])]});
            var Q1;
            Q1=makeQuery(id+"F116.imprint","IMPRINT",FACE,{"disambiguationData":[TD([[makeQuery(id+"F116.imprint","IMPRINT",EDGE,{"derivedFrom":sQuery(id+"F116.wireOp",EDGE,"E232")}),1.0]])]});
            var Q2;
            Q2=makeQuery(id+"F116.imprint","IMPRINT",FACE,{"disambiguationData":[TD([[makeQuery(id+"F116.imprint","IMPRINT",EDGE,{"derivedFrom":sQuery(id+"F116.wireOp",EDGE,"E231")}),1.0]])]});
            var Q3;
            Q3=makeQuery(id+"F116.imprint","IMPRINT",FACE,{"disambiguationData":[TD([[makeQuery(id+"F116.imprint","IMPRINT",EDGE,{"derivedFrom":sQuery(id+"F116.wireOp",EDGE,"E230")}),1.0]])]});
            extrude(context, id + "F117", {"entities" : qUnion([Q0, Q1, Q2, Q3]), "operationType" : NewBodyOperationType.REMOVE, "oppositeDirection" : true, "depth" : 2.8 * mm});
        }
        {
            var Q0;
            Q0=makeQuery(id+"F103.opExtrude","CAP_FACE",FACE,{"disambiguationData":[OSD([sQuery(id+"F102.wireOp",EDGE,"E222")])],"isStart":false});
            var sketch = newSketch(context, id + "F118", { "sketchPlane" : qUnion([Q0])});
            skCircle(sketch, "E233", {"center": v(-75.7, -1.89) * mm, "radius": 0.45 * mm});
            skCircle(sketch, "E234", {"center": v(-74.47, -3.23) * mm, "radius": 0.45 * mm});
            skCircle(sketch, "E235", {"center": v(-75.7, -4.46) * mm, "radius": 0.45 * mm});
            skCircle(sketch, "E236", {"center": v(-77.06, -3.23) * mm, "radius": 0.44 * mm});
            skSolve(sketch);
        }
        {
            var Q0;
            Q0=makeQuery(id+"F118.imprint","IMPRINT",FACE,{"disambiguationData":[TD([[makeQuery(id+"F118.imprint","IMPRINT",EDGE,{"derivedFrom":sQuery(id+"F118.wireOp",EDGE,"E234")}),1.0]])]});
            var Q1;
            Q1=makeQuery(id+"F118.imprint","IMPRINT",FACE,{"disambiguationData":[TD([[makeQuery(id+"F118.imprint","IMPRINT",EDGE,{"derivedFrom":sQuery(id+"F118.wireOp",EDGE,"E236")}),1.0]])]});
            var Q2;
            Q2=makeQuery(id+"F118.imprint","IMPRINT",FACE,{"disambiguationData":[TD([[makeQuery(id+"F118.imprint","IMPRINT",EDGE,{"derivedFrom":sQuery(id+"F118.wireOp",EDGE,"E235")}),1.0]])]});
            var Q3;
            Q3=makeQuery(id+"F118.imprint","IMPRINT",FACE,{"disambiguationData":[TD([[makeQuery(id+"F118.imprint","IMPRINT",EDGE,{"derivedFrom":sQuery(id+"F118.wireOp",EDGE,"E233")}),1.0]])]});
            extrude(context, id + "F119", {"entities" : qUnion([Q0, Q1, Q2, Q3]), "operationType" : NewBodyOperationType.REMOVE, "oppositeDirection" : true, "depth" : 3.43 * mm});
        }
        {
            var Q0;
            Q0=makeQuery(id+"F94.opExtrude","CAP_FACE",FACE,{"disambiguationData":[OSD([sQuery(id+"F93.wireOp",EDGE,"E216")])],"isStart":false});
            var sketch = newSketch(context, id + "F120", { "sketchPlane" : qUnion([Q0])});
            skPoint(sketch, "E237.startSnap0", {"position": v(-14.51, -3.52) * mm});
            skCircle(sketch, "E238", {"center": v(-13.24, -3.52) * mm, "radius": 0.45 * mm});
            skCircle(sketch, "E239", {"center": v(-14.51, -4.75) * mm, "radius": 0.44 * mm});
            skCircle(sketch, "E240", {"center": v(-15.8, -3.52) * mm, "radius": 0.45 * mm});
            skCircle(sketch, "E241", {"center": v(-14.51, -2.3) * mm, "radius": 0.4 * mm});
            skSolve(sketch);
        }
        {
            var Q0;
            Q0=makeQuery(id+"F120.imprint","IMPRINT",FACE,{"disambiguationData":[TD([[makeQuery(id+"F120.imprint","IMPRINT",EDGE,{"derivedFrom":sQuery(id+"F120.wireOp",EDGE,"E238")}),1.0]])]});
            var Q1;
            Q1=makeQuery(id+"F120.imprint","IMPRINT",FACE,{"disambiguationData":[TD([[makeQuery(id+"F120.imprint","IMPRINT",EDGE,{"derivedFrom":sQuery(id+"F120.wireOp",EDGE,"E241")}),1.0]])]});
            var Q2;
            Q2=makeQuery(id+"F120.imprint","IMPRINT",FACE,{"disambiguationData":[TD([[makeQuery(id+"F120.imprint","IMPRINT",EDGE,{"derivedFrom":sQuery(id+"F120.wireOp",EDGE,"E240")}),1.0]])]});
            var Q3;
            Q3=makeQuery(id+"F120.imprint","IMPRINT",FACE,{"disambiguationData":[TD([[makeQuery(id+"F120.imprint","IMPRINT",EDGE,{"derivedFrom":sQuery(id+"F120.wireOp",EDGE,"E239")}),1.0]])]});
            extrude(context, id + "F121", {"entities" : qUnion([Q0, Q1, Q2, Q3]), "operationType" : NewBodyOperationType.REMOVE, "oppositeDirection" : true, "depth" : 2.54 * mm});
        }
        {
            var Q0;
            Q0=makeQuery(id+"F99.opExtrude","CAP_FACE",FACE,{"disambiguationData":[OSD([sQuery(id+"F98.wireOp",EDGE,"E220")])],"isStart":false});
            var sketch = newSketch(context, id + "F122", { "sketchPlane" : qUnion([Q0])});
            skCircle(sketch, "E242", {"center": v(14.5, -2.25) * mm, "radius": 0.43 * mm});
            skCircle(sketch, "E243", {"center": v(15.8, -3.49) * mm, "radius": 0.43 * mm});
            skCircle(sketch, "E244", {"center": v(14.5, -4.74) * mm, "radius": 0.43 * mm});
            skCircle(sketch, "E245", {"center": v(13.26, -3.49) * mm, "radius": 0.43 * mm});
            skSolve(sketch);
        }
        {
            var Q0;
            Q0=makeQuery(id+"F122.imprint","IMPRINT",FACE,{"disambiguationData":[TD([[makeQuery(id+"F122.imprint","IMPRINT",EDGE,{"derivedFrom":sQuery(id+"F122.wireOp",EDGE,"E243")}),1.0]])]});
            var Q1;
            Q1=makeQuery(id+"F122.imprint","IMPRINT",FACE,{"disambiguationData":[TD([[makeQuery(id+"F122.imprint","IMPRINT",EDGE,{"derivedFrom":sQuery(id+"F122.wireOp",EDGE,"E242")}),1.0]])]});
            var Q2;
            Q2=makeQuery(id+"F122.imprint","IMPRINT",FACE,{"disambiguationData":[TD([[makeQuery(id+"F122.imprint","IMPRINT",EDGE,{"derivedFrom":sQuery(id+"F122.wireOp",EDGE,"E245")}),1.0]])]});
            var Q3;
            Q3=makeQuery(id+"F122.imprint","IMPRINT",FACE,{"disambiguationData":[TD([[makeQuery(id+"F122.imprint","IMPRINT",EDGE,{"derivedFrom":sQuery(id+"F122.wireOp",EDGE,"E244")}),1.0]])]});
            extrude(context, id + "F123", {"entities" : qUnion([Q0, Q1, Q2, Q3]), "operationType" : NewBodyOperationType.REMOVE, "oppositeDirection" : true, "depth" : 3.56 * mm});
        }
        {
            var Q0;
            Q0=makeQuery(id+"F76.opExtrude","CAP_EDGE",EDGE,{"disambiguationData":[OSD([sQuery(id+"F75.wireOp",EDGE,"E189")])],"isStart":false});
            var Q1;
            Q1=makeQuery(id+"F76.opExtrude","CAP_EDGE",EDGE,{"disambiguationData":[OSD([sQuery(id+"F75.wireOp",EDGE,"E187")])],"isStart":false});
            var Q2;
            Q2=makeQuery(id+"F76.opExtrude","CAP_EDGE",EDGE,{"disambiguationData":[OSD([sQuery(id+"F75.wireOp",EDGE,"E191")])],"isStart":false});
            var Q3;
            Q3=makeQuery(id+"F76.opExtrude","CAP_EDGE",EDGE,{"disambiguationData":[OSD([sQuery(id+"F75.wireOp",EDGE,"E184")])],"isStart":false});
            var Q4;
            Q4=makeQuery(id+"F76.opExtrude","CAP_EDGE",EDGE,{"disambiguationData":[OSD([sQuery(id+"F75.wireOp",EDGE,"E186")])],"isStart":false});
            var Q5;
            Q5=makeQuery(id+"F76.opExtrude","CAP_EDGE",EDGE,{"disambiguationData":[OSD([sQuery(id+"F75.wireOp",EDGE,"E182")])],"isStart":false});
            fillet(context, id + "F124", {"entities" : qUnion([Q0, Q1, Q2, Q3, Q4, Q5]), "radius" : 0.25 * mm, "tangentPropagation" : true, "allowEdgeOverflow" : false});
        }
        {
            var Q0;
            Q0=makeQuery(id+"F2.opExtrude","CAP_EDGE",EDGE,{"disambiguationData":[OSD([sQuery(id+"F0.wireOp",EDGE,"E9")])],"isStart":false});
            var Q1;
            Q1=makeQuery(id+"F1.opExtrude","CAP_EDGE",EDGE,{"disambiguationData":[OSD([sQuery(id+"F0.wireOp",EDGE,"E9")])],"isStart":false});
            var Q2;
            Q2=makeQuery(id+"F2.opExtrude","CAP_EDGE",EDGE,{"disambiguationData":[OSD([sQuery(id+"F0.wireOp",EDGE,"E6")])],"isStart":false});
            var Q3;
            {var subQ0=sQuery(id+"F0.wireOp",EDGE,"E6");Q3=makeQuery(id+"F5.opShell","OFFSET_EDGE",EDGE,{"disambiguationData":[OSD([subQ0]),TDD([makeQuery(id+"F2.opExtrude","CAP_EDGE",EDGE,{"disambiguationData":[OSD([subQ0])],"isStart":false})]),OD(0.0)]});}
            var Q4;
            {var subQ0=sQuery(id+"F0.wireOp",EDGE,"E6");Q4=makeQuery(id+"F5.opShell","OFFSET_EDGE",EDGE,{"disambiguationData":[OSD([subQ0]),TDD([makeQuery(id+"F1.opExtrude","CAP_EDGE",EDGE,{"disambiguationData":[OSD([subQ0])],"isStart":false})]),OD(0.0)]});}
            var Q5;
            {var subQ0=sQuery(id+"F0.wireOp",EDGE,"E6");var subQ1=sQuery(id+"F0.wireOp",EDGE,"E5");Q5=makeQuery(id+"F2.boolean.opBoolean","MERGE",EDGE,{"derivedFrom":[makeQuery(id+"F1.opExtrude","SWEPT_EDGE",EDGE,{"disambiguationData":[OSD([subQ1,subQ0])]}),makeQuery(id+"F2.opExtrude","SWEPT_EDGE",EDGE,{"disambiguationData":[OSD([subQ1,subQ0])]})]});}
            var Q6;
            Q6=makeQuery(id+"F5.opShell","OFFSET_EDGE",EDGE,{"disambiguationData":[OSD([sQuery(id+"F0.wireOp",EDGE,"E5"),sQuery(id+"F0.wireOp",EDGE,"E6")])]});
            var Q7;
            Q7=makeQuery(id+"F1.opExtrude","CAP_EDGE",EDGE,{"disambiguationData":[OSD([sQuery(id+"F0.wireOp",EDGE,"E6")])],"isStart":false});
            fillet(context, id + "F125", {"entities" : qUnion([Q0, Q1, Q2, Q3, Q4, Q5, Q6, Q7]), "radius" : 0.25 * mm, "tangentPropagation" : true, "allowEdgeOverflow" : false});
        }
        {
            var Q0;
            Q0=makeQuery(id+"F73.imprint","IMPRINT",FACE,{"disambiguationData":[TD([[makeQuery(id+"F73.imprint","IMPRINT",EDGE,{"derivedFrom":sQuery(id+"F73.wireOp",EDGE,"E178")}),-1.0]])]});
            var sketch = newSketch(context, id + "F126", { "sketchPlane" : qUnion([Q0])});
            skCircle(sketch, "E246", {"center": v(-88.72, -3.15) * mm, "radius": 1.7 * mm});
            skSolve(sketch);
        }
        {
            var Q0;
            Q0=makeQuery(id+"F126.imprint","IMPRINT",FACE,{"disambiguationData":[TD([[makeQuery(id+"F126.imprint","IMPRINT",EDGE,{"derivedFrom":sQuery(id+"F126.wireOp",EDGE,"E246")}),1.0]])]});
            extrude(context, id + "F127", {"entities" : qUnion([Q0]), "oppositeDirection" : true, "depth" : 16 * mm});
        }
        {
            var Q0;
            {var subQ1=sQuery(id+"F0.wireOp",EDGE,"E1");var subQ3=sQuery(id+"F0.wireOp",EDGE,"E19");var subQ5=sQuery(id+"F0.wireOp",EDGE,"E16");var subQ10=sQuery(id+"F0.wireOp",EDGE,"E17");var subQ26=sQuery(id+"F0.wireOp",EDGE,"E11");var subQ33=sQuery(id+"F0.wireOp",EDGE,"E4");var subQ34=sQuery(id+"F0.wireOp",EDGE,"E0");var subQ41=sQuery(id+"F0.wireOp",EDGE,"E24");Q0=makeQuery(id+"F90.boolean.opBoolean","SPLIT",FACE,{"disambiguationData":[TD([makeQuery(id+"F1.opExtrude","SWEPT_FACE",FACE,{"disambiguationData":[OSD([subQ1])]})])],"derivedFrom":makeQuery(id+"F14.boolean.opBoolean","MERGE",FACE,{"derivedFrom":[makeQuery(id+"F13.boolean.opBoolean","MERGE",FACE,{"derivedFrom":[makeQuery(id+"F11.boolean.opBoolean","MERGE",FACE,{"derivedFrom":[makeQuery(id+"F10.boolean.opBoolean","MERGE",FACE,{"derivedFrom":[makeQuery(id+"F4.boolean.opBoolean","MERGE",FACE,{"derivedFrom":[makeQuery(id+"F3.boolean.opBoolean","MERGE",FACE,{"derivedFrom":[makeQuery(id+"F2.boolean.opBoolean","MERGE",FACE,{"derivedFrom":[makeQuery(id+"F1.opExtrude","SWEPT_FACE",FACE,{"disambiguationData":[OSD([subQ34])]}),makeQuery(id+"F2.opExtrude","SWEPT_FACE",FACE,{"disambiguationData":[OSD([subQ34])]})]}),makeQuery(id+"F2.boolean.opBoolean","MERGE",FACE,{"derivedFrom":[makeQuery(id+"F1.opExtrude","SWEPT_FACE",FACE,{"disambiguationData":[OSD([subQ33])]}),makeQuery(id+"F2.opExtrude","SWEPT_FACE",FACE,{"disambiguationData":[OSD([subQ33])]})]}),makeQuery(id+"F2.boolean.opBoolean","MERGE",FACE,{"derivedFrom":[makeQuery(id+"F1.opExtrude","SWEPT_FACE",FACE,{"disambiguationData":[OSD([subQ26])]}),makeQuery(id+"F2.opExtrude","SWEPT_FACE",FACE,{"disambiguationData":[OSD([subQ26])]})]}),makeQuery(id+"F3.opExtrude","SWEPT_FACE",FACE,{"disambiguationData":[OSD([subQ5])]}),makeQuery(id+"F3.opExtrude","SWEPT_FACE",FACE,{"disambiguationData":[OSD([subQ10])]})]}),makeQuery(id+"F4.opExtrude","SWEPT_FACE",FACE,{"disambiguationData":[OSD([subQ5])]}),makeQuery(id+"F4.opExtrude","SWEPT_FACE",FACE,{"disambiguationData":[OSD([subQ10])]})]}),makeQuery(id+"F10.opExtrude","SWEPT_FACE",FACE,{"disambiguationData":[OSD([subQ3])]})]}),makeQuery(id+"F11.opExtrude","SWEPT_FACE",FACE,{"disambiguationData":[OSD([subQ3])]})]}),makeQuery(id+"F13.opExtrude","SWEPT_FACE",FACE,{"disambiguationData":[OSD([subQ41])]})]}),makeQuery(id+"F14.opExtrude","SWEPT_FACE",FACE,{"disambiguationData":[OSD([subQ41])]})]})});}
            var sketch = newSketch(context, id + "F128", { "sketchPlane" : qUnion([Q0])});
            skLineSegment(sketch, "E247", {"start": v(90.5, -11.36) * mm, "end": v(90.41, -9.38) * mm});
            skLineSegment(sketch, "E248", {"start": v(90.5, -11.36) * mm, "end": v(79.17, -11.36) * mm});
            skLineSegment(sketch, "E249", {"start": v(90.41, -9.38) * mm, "end": v(79.17, -9.38) * mm});
            skLineSegment(sketch, "E250", {"start": v(79.17, -9.38) * mm, "end": v(79.17, -11.36) * mm});
            skSolve(sketch);
        }
        {
            var Q0;
            Q0=makeQuery(id+"F128.imprint","IMPRINT",FACE,{"disambiguationData":[TD([[makeQuery(id+"F128.imprint","IMPRINT",EDGE,{"derivedFrom":sQuery(id+"F128.wireOp",EDGE,"gfzSgjeb-P8uS-lJTb-qpUj-fK5AdrdcNk0x")}),1.0]])]});
            var Q1;
            {var subQ0=sQuery(id+"F128.wireOp",EDGE,"E247");Q1=makeQuery(id+"F128.imprint","IMPRINT",FACE,{"disambiguationData":[TD([[makeQuery(id+"F128.imprint","IMPRINT",EDGE,{"derivedFrom":subQ0}),1.0]])]});}
            extrude(context, id + "F129", {"entities" : qUnion([Q0, Q1]), "depth" : 4.6 * mm});
        }
        {
            var Q0;
            Q0=makeQuery(id+"F129.opExtrude","CAP_EDGE",EDGE,{"disambiguationData":[OSD([sQuery(id+"F128.wireOp",EDGE,"E249")])],"isStart":false});
            var Q1;
            Q1=makeQuery(id+"F129.opExtrude","CAP_FACE",FACE,{"disambiguationData":[OSD([sQuery(id+"F0.wireOp",EDGE,"E16"),sQuery(id+"F87.wireOp",EDGE,"E205"),sQuery(id+"F87.wireOp",EDGE,"E206"),sQuery(id+"F128.wireOp",EDGE,"E247"),sQuery(id+"F128.wireOp",EDGE,"E248"),sQuery(id+"F128.wireOp",EDGE,"E249")])],"isStart":false});
            var Q2;
            Q2=makeQuery(id+"F129.opExtrude","SWEPT_EDGE",EDGE,{"disambiguationData":[OSD([sQuery(id+"F0.wireOp",EDGE,"E16"),sQuery(id+"F87.wireOp",EDGE,"E205"),sQuery(id+"F87.wireOp",EDGE,"E206"),sQuery(id+"F128.wireOp",EDGE,"E249")])]});
            var Q3;
            Q3=makeQuery(id+"F129.opExtrude","SWEPT_EDGE",EDGE,{"disambiguationData":[OSD([sQuery(id+"F128.wireOp",EDGE,"E247"),sQuery(id+"F128.wireOp",EDGE,"E249")])]});
            var Q4;
            Q4=makeQuery(id+"F129.opExtrude","SWEPT_EDGE",EDGE,{"disambiguationData":[OSD([sQuery(id+"F128.wireOp",EDGE,"E247"),sQuery(id+"F128.wireOp",EDGE,"E248")])]});
            var Q5;
            Q5=makeQuery(id+"F129.opExtrude","SWEPT_EDGE",EDGE,{"disambiguationData":[OSD([sQuery(id+"F0.wireOp",EDGE,"E16"),sQuery(id+"F87.wireOp",EDGE,"E205"),sQuery(id+"F87.wireOp",EDGE,"E206"),sQuery(id+"F128.wireOp",EDGE,"E248")])]});
            fillet(context, id + "F130", {"entities" : qUnion([Q0, Q1, Q2, Q3, Q4, Q5]), "radius" : 0.76 * mm, "tangentPropagation" : true, "allowEdgeOverflow" : false});
        }
        {
            var Q0;
            {var subQ1=sQuery(id+"F0.wireOp",EDGE,"E1");var subQ3=sQuery(id+"F0.wireOp",EDGE,"E19");var subQ5=sQuery(id+"F0.wireOp",EDGE,"E16");var subQ10=sQuery(id+"F0.wireOp",EDGE,"E17");var subQ26=sQuery(id+"F0.wireOp",EDGE,"E11");var subQ33=sQuery(id+"F0.wireOp",EDGE,"E4");var subQ34=sQuery(id+"F0.wireOp",EDGE,"E0");var subQ41=sQuery(id+"F0.wireOp",EDGE,"E24");Q0=makeQuery(id+"F90.boolean.opBoolean","SPLIT",FACE,{"disambiguationData":[TD([makeQuery(id+"F1.opExtrude","SWEPT_FACE",FACE,{"disambiguationData":[OSD([subQ1])]})])],"derivedFrom":makeQuery(id+"F14.boolean.opBoolean","MERGE",FACE,{"derivedFrom":[makeQuery(id+"F13.boolean.opBoolean","MERGE",FACE,{"derivedFrom":[makeQuery(id+"F11.boolean.opBoolean","MERGE",FACE,{"derivedFrom":[makeQuery(id+"F10.boolean.opBoolean","MERGE",FACE,{"derivedFrom":[makeQuery(id+"F4.boolean.opBoolean","MERGE",FACE,{"derivedFrom":[makeQuery(id+"F3.boolean.opBoolean","MERGE",FACE,{"derivedFrom":[makeQuery(id+"F2.boolean.opBoolean","MERGE",FACE,{"derivedFrom":[makeQuery(id+"F1.opExtrude","SWEPT_FACE",FACE,{"disambiguationData":[OSD([subQ34])]}),makeQuery(id+"F2.opExtrude","SWEPT_FACE",FACE,{"disambiguationData":[OSD([subQ34])]})]}),makeQuery(id+"F2.boolean.opBoolean","MERGE",FACE,{"derivedFrom":[makeQuery(id+"F1.opExtrude","SWEPT_FACE",FACE,{"disambiguationData":[OSD([subQ33])]}),makeQuery(id+"F2.opExtrude","SWEPT_FACE",FACE,{"disambiguationData":[OSD([subQ33])]})]}),makeQuery(id+"F2.boolean.opBoolean","MERGE",FACE,{"derivedFrom":[makeQuery(id+"F1.opExtrude","SWEPT_FACE",FACE,{"disambiguationData":[OSD([subQ26])]}),makeQuery(id+"F2.opExtrude","SWEPT_FACE",FACE,{"disambiguationData":[OSD([subQ26])]})]}),makeQuery(id+"F3.opExtrude","SWEPT_FACE",FACE,{"disambiguationData":[OSD([subQ5])]}),makeQuery(id+"F3.opExtrude","SWEPT_FACE",FACE,{"disambiguationData":[OSD([subQ10])]})]}),makeQuery(id+"F4.opExtrude","SWEPT_FACE",FACE,{"disambiguationData":[OSD([subQ5])]}),makeQuery(id+"F4.opExtrude","SWEPT_FACE",FACE,{"disambiguationData":[OSD([subQ10])]})]}),makeQuery(id+"F10.opExtrude","SWEPT_FACE",FACE,{"disambiguationData":[OSD([subQ3])]})]}),makeQuery(id+"F11.opExtrude","SWEPT_FACE",FACE,{"disambiguationData":[OSD([subQ3])]})]}),makeQuery(id+"F13.opExtrude","SWEPT_FACE",FACE,{"disambiguationData":[OSD([subQ41])]})]}),makeQuery(id+"F14.opExtrude","SWEPT_FACE",FACE,{"disambiguationData":[OSD([subQ41])]})]})});}
            var sketch = newSketch(context, id + "F131", { "sketchPlane" : qUnion([Q0])});
            skLineSegment(sketch, "E251.bottom", {"start": v(56.23, -8.24) * mm, "end": v(40.36, -8.24) * mm});
            skLineSegment(sketch, "E251.top", {"start": v(56.23, -16.92) * mm, "end": v(40.36, -16.92) * mm});
            skLineSegment(sketch, "E251.left", {"start": v(56.23, -8.24) * mm, "end": v(56.23, -16.92) * mm});
            skLineSegment(sketch, "E251.right", {"start": v(40.36, -8.24) * mm, "end": v(40.36, -16.92) * mm});
            skSolve(sketch);
        }
        {
            var Q0;
            Q0=makeQuery(id+"F131.imprint","IMPRINT",FACE,{"disambiguationData":[TD([[makeQuery(id+"F131.imprint","IMPRINT",EDGE,{"derivedFrom":sQuery(id+"F131.wireOp",EDGE,"E251.bottom")}),1.0]])]});
            extrude(context, id + "F132", {"entities" : qUnion([Q0]), "operationType" : NewBodyOperationType.ADD, "depth" : 2.54 * mm});
        }
        {
            var Q0;
            Q0=makeQuery(id+"F132.opExtrude","CAP_EDGE",EDGE,{"disambiguationData":[OSD([sQuery(id+"F131.wireOp",EDGE,"E251.right")])],"isStart":false});
            var Q1;
            Q1=makeQuery(id+"F132.opExtrude","CAP_EDGE",EDGE,{"disambiguationData":[OSD([sQuery(id+"F131.wireOp",EDGE,"E251.left")])],"isStart":false});
            var Q2;
            Q2=makeQuery(id+"F132.opExtrude","CAP_EDGE",EDGE,{"disambiguationData":[OSD([sQuery(id+"F131.wireOp",EDGE,"E251.top")])],"isStart":false});
            var Q3;
            Q3=makeQuery(id+"F132.opExtrude","CAP_EDGE",EDGE,{"disambiguationData":[OSD([sQuery(id+"F131.wireOp",EDGE,"E251.bottom")])],"isStart":false});
            fillet(context, id + "F133", {"entities" : qUnion([Q0, Q1, Q2, Q3]), "radius" : 2.54 * mm, "tangentPropagation" : true, "allowEdgeOverflow" : false});
        }
    });
